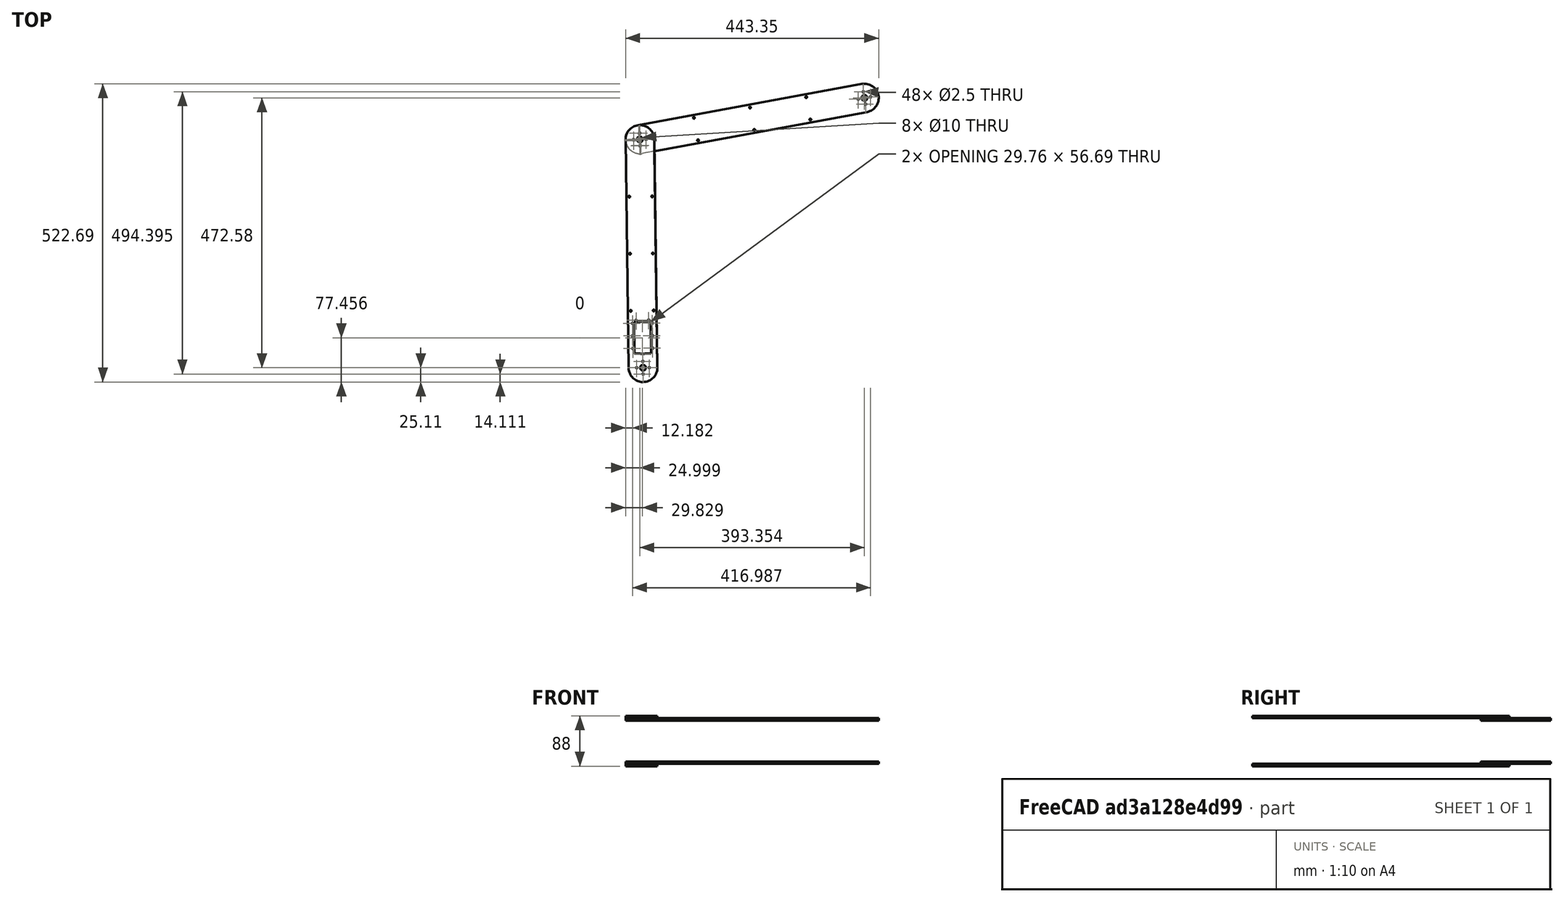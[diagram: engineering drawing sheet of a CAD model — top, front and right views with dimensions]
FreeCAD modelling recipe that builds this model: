
FCSTD DOCUMENT  (FreeCAD 1.0R39109 (Git))
Label: arm_assembly4
License: All rights reserved
LicenseURL: https://en.wikipedia.org/wiki/All_rights_reserved
objects: App::FeaturePython×14, App::Link×8, Sketcher::SketchObject×4, PartDesign::Pad×4, PartDesign::Body×4, Assembly::JointGroup×1, Assembly::AssemblyObject×1
note: 24 computed .brp shape members not serialized (recipe doc carries the construction recipe); baked Part::Feature solids carry a one-line shape summary decoded from their .brp
EXTERNAL_REF file=srv.FCStd obj=Part__Feature
EXTERNAL_REF file=pulleys/gt2_24T_pulley_open.FCStd obj=Body
EXTERNAL_REF file=pulleys/gt2_48T_pulley.FCStd obj=Body
EXTERNAL_REF file=pulleys/gt2_48T_pulley_double.FCStd obj=Body

FEATURE [Sketcher::SketchObject] Sketch
  ArcFitTolerance = 1e-06
  AttachmentSupport = -> [XY_Plane]
  FullyConstrained = false
  MakeInternals = false
  MapMode = 5
  sketch-geometry (67):
    g0: LineSegment [constr] StartX=1.5008e-12 StartY=20 StartZ=0 EndX=1.5008e-12 EndY=-20 EndZ=0
    g1: LineSegment [constr] StartX=-2.359e-12 StartY=0 StartZ=0 EndX=-2.359e-12 EndY=400 EndZ=0
    g2: LineSegment [constr] StartX=1.5008e-12 StartY=20 StartZ=0 EndX=1.5008e-12 EndY=25 EndZ=0
    g3: Circle CenterX=-2.359e-12 CenterY=400 CenterZ=0 NormalX=0 NormalY=0 NormalZ=1 AngleXU=0 Radius=5
    g4: Circle CenterX=-2.359e-12 CenterY=400 CenterZ=0 NormalX=0 NormalY=0 NormalZ=1 AngleXU=0 Radius=2
    g5: Circle CenterX=-10.9997 CenterY=400 CenterZ=0 NormalX=0 NormalY=0 NormalZ=1 AngleXU=0 Radius=1.25
    g6: Circle CenterX=0 CenterY=389 CenterZ=0 NormalX=0 NormalY=0 NormalZ=1 AngleXU=0 Radius=1.25
    g7: Circle CenterX=10.9997 CenterY=400 CenterZ=0 NormalX=0 NormalY=0 NormalZ=1 AngleXU=0 Radius=1.25
    g8: Circle CenterX=0 CenterY=411 CenterZ=0 NormalX=0 NormalY=0 NormalZ=1 AngleXU=0 Radius=1.25
    g9: LineSegment [constr] StartX=0 StartY=-5 StartZ=0 EndX=0 EndY=5.99996 EndZ=0
    g10: Circle [constr] CenterX=0 CenterY=0 CenterZ=0 NormalX=0 NormalY=0 NormalZ=1 AngleXU=0 Radius=14
    g11: LineSegment [constr] StartX=0 StartY=0 StartZ=0 EndX=25.23 EndY=0 EndZ=0
    g12: Circle [constr] CenterX=0 CenterY=-3.8e-05 CenterZ=0 NormalX=0 NormalY=0 NormalZ=1 AngleXU=0 Radius=11
    g13: Circle CenterX=0 CenterY=0 CenterZ=0 NormalX=0 NormalY=0 NormalZ=1 AngleXU=0 Radius=5
    g14: Circle CenterX=10.9997 CenterY=0 CenterZ=0 NormalX=0 NormalY=0 NormalZ=1 AngleXU=0 Radius=1.25
    g15: Circle CenterX=-10.9997 CenterY=0 CenterZ=0 NormalX=0 NormalY=0 NormalZ=1 AngleXU=0 Radius=1.25
    g16: Circle CenterX=0 CenterY=-10.9997 CenterZ=0 NormalX=0 NormalY=0 NormalZ=1 AngleXU=0 Radius=1.25
    g17: Circle CenterX=0 CenterY=11 CenterZ=0 NormalX=0 NormalY=0 NormalZ=1 AngleXU=0 Radius=1.25
    g18: LineSegment [constr] StartX=0 StartY=0 StartZ=0 EndX=-25 EndY=0 EndZ=0
    g19: LineSegment [constr] StartX=20.1368 StartY=86.0999 StartZ=0 EndX=20.1368 EndY=24.9999 EndZ=0
    g20: LineSegment [constr] StartX=0.036848 StartY=80.5 StartZ=0 EndX=14.5368 EndY=80.5 EndZ=0
    g21: LineSegment StartX=14.5368 StartY=80.5 StartZ=0 EndX=-14.4632 EndY=80.5 EndZ=0
    g22: LineSegment StartX=14.5368 StartY=80.5 StartZ=0 EndX=14.5368 EndY=24.9999 EndZ=0
    g23: Circle CenterX=11.0368 CenterY=83.3 CenterZ=0 NormalX=0 NormalY=0 NormalZ=1 AngleXU=0 Radius=1.25
    g24: Circle CenterX=17.3368 CenterY=78 CenterZ=0 NormalX=0 NormalY=0 NormalZ=1 AngleXU=0 Radius=1.25
    g25: LineSegment [constr] StartX=-20.0632 StartY=86.0999 StartZ=0 EndX=20.1368 EndY=86.0999 EndZ=0
    g26: Circle CenterX=17.3368 CenterY=56 CenterZ=0 NormalX=0 NormalY=0 NormalZ=1 AngleXU=0 Radius=1.25
    g27: Circle CenterX=17.3368 CenterY=34 CenterZ=0 NormalX=0 NormalY=0 NormalZ=1 AngleXU=0 Radius=1.25
    g28: Circle [constr] CenterX=0.036848 CenterY=37.9999 CenterZ=0 NormalX=0 NormalY=0 NormalZ=1 AngleXU=0 Radius=14
    g29: ArcOfCircle CenterX=0.036848 CenterY=37.9999 CenterZ=0 NormalX=0 NormalY=0 NormalZ=1 AngleXU=0 Radius=14 StartAngle=4.33214 EndAngle=5.09264
    g30: LineSegment StartX=5.233 StartY=24.9999 StartZ=0 EndX=14.5368 EndY=24.9999 EndZ=0
    g31: LineSegment [constr] StartX=14.5368 StartY=24.9999 StartZ=0 EndX=20.1368 EndY=24.9999 EndZ=0
    g32: LineSegment [constr] StartX=17.3368 StartY=56 StartZ=0 EndX=-17.2632 EndY=56 EndZ=0
    g33: LineSegment [constr] StartX=-20.0632 StartY=24.9999 StartZ=0 EndX=-20.0632 EndY=86.0999 EndZ=0
    g34: LineSegment StartX=-14.4632 StartY=80.5 StartZ=0 EndX=-14.4632 EndY=24.9999 EndZ=0
    g35: Circle CenterX=-17.2632 CenterY=78 CenterZ=0 NormalX=0 NormalY=0 NormalZ=1 AngleXU=0 Radius=1.25
    g36: Circle CenterX=-10.9632 CenterY=83.3 CenterZ=0 NormalX=0 NormalY=0 NormalZ=1 AngleXU=0 Radius=1.25
    g37: Circle CenterX=-17.2632 CenterY=56 CenterZ=0 NormalX=0 NormalY=0 NormalZ=1 AngleXU=0 Radius=1.25
    g38: Circle CenterX=-17.2632 CenterY=34 CenterZ=0 NormalX=0 NormalY=0 NormalZ=1 AngleXU=0 Radius=1.25
    g39: LineSegment StartX=-14.4632 StartY=24.9999 StartZ=0 EndX=-5.15931 EndY=24.9999 EndZ=0
    g40: LineSegment [constr] StartX=-20.0632 StartY=24.9999 StartZ=0 EndX=-14.4632 EndY=24.9999 EndZ=0
    g41: ArcOfCircle CenterX=0.115002 CenterY=3.75548e-06 CenterZ=0 NormalX=0 NormalY=0 NormalZ=1 AngleXU=0 Radius=25.115 StartAngle=3.14159 EndAngle=6.28319
    g42: ArcOfCircle CenterX=0.115002 CenterY=399.959 CenterZ=0 NormalX=0 NormalY=0 NormalZ=1 AngleXU=0 Radius=25.115 StartAngle=0 EndAngle=3.14159
    g43: LineSegment StartX=-25 StartY=3.75548e-06 StartZ=0 EndX=-25 EndY=399.959 EndZ=0
    g44: LineSegment StartX=25.23 StartY=3.75548e-06 StartZ=0 EndX=25.23 EndY=399.959 EndZ=0
    g45: LineSegment [constr] StartX=25.23 StartY=199.98 StartZ=0 EndX=-25 EndY=199.98 EndZ=0
    g46: LineSegment [constr] StartX=25.23 StartY=199.98 StartZ=0 EndX=55.23 EndY=199.98 EndZ=0
    g47: LineSegment [constr] StartX=25.23 StartY=0 StartZ=0 EndX=55.23 EndY=0 EndZ=0
    g48: LineSegment [constr] StartX=55.23 StartY=0 StartZ=0 EndX=55.23 EndY=199.98 EndZ=0
    g49: LineSegment [constr] StartX=55.23 StartY=99.9898 StartZ=0 EndX=25.23 EndY=99.9898 EndZ=0
    g50: LineSegment [constr] StartX=25.23 StartY=99.9898 StartZ=0 EndX=-25 EndY=99.9898 EndZ=0
    g51: LineSegment [constr] StartX=25.23 StartY=399.959 StartZ=0 EndX=55.23 EndY=399.959 EndZ=0
    g52: LineSegment [constr] StartX=55.23 StartY=399.959 StartZ=0 EndX=55.23 EndY=199.98 EndZ=0
    g53: LineSegment [constr] StartX=55.23 StartY=299.969 StartZ=0 EndX=25.23 EndY=299.969 EndZ=0
    g54: LineSegment [constr] StartX=25.23 StartY=299.969 StartZ=0 EndX=-25 EndY=299.969 EndZ=0
    g55: LineSegment [constr] StartX=-25 StartY=299.969 StartZ=0 EndX=-20 EndY=299.969 EndZ=0
    g56: LineSegment [constr] StartX=-20 StartY=299.969 StartZ=0 EndX=-20 EndY=199.98 EndZ=0
    g57: LineSegment [constr] StartX=-20 StartY=199.98 StartZ=0 EndX=-20 EndY=99.9898 EndZ=0
    g58: LineSegment [constr] StartX=25.23 StartY=299.969 StartZ=0 EndX=20.23 EndY=299.969 EndZ=0
    g59: LineSegment [constr] StartX=20.23 StartY=299.969 StartZ=0 EndX=20.23 EndY=199.98 EndZ=0
    g60: LineSegment [constr] StartX=20.23 StartY=199.98 StartZ=0 EndX=20.23 EndY=99.9898 EndZ=0
    g61: Circle CenterX=-20 CenterY=299.969 CenterZ=0 NormalX=0 NormalY=0 NormalZ=1 AngleXU=0 Radius=1.5
    g62: Circle CenterX=20.23 CenterY=299.969 CenterZ=0 NormalX=0 NormalY=0 NormalZ=1 AngleXU=0 Radius=1.5
    g63: Circle CenterX=-20 CenterY=199.98 CenterZ=0 NormalX=0 NormalY=0 NormalZ=1 AngleXU=0 Radius=1.5
    g64: Circle CenterX=20.23 CenterY=199.98 CenterZ=0 NormalX=0 NormalY=0 NormalZ=1 AngleXU=0 Radius=1.5
    g65: Circle CenterX=-20 CenterY=99.9898 CenterZ=0 NormalX=0 NormalY=0 NormalZ=1 AngleXU=0 Radius=1.5
    g66: Circle CenterX=20.23 CenterY=99.9898 CenterZ=0 NormalX=0 NormalY=0 NormalZ=1 AngleXU=0 Radius=1.5
  constraints (132):
    c: Vertical(g0)
    c: Vertical(g1)
    c: Coincident(g2,g0)
    c: Vertical(g2)
    c: Diameter(g3) = 10
    c: Coincident(g3,g1)
    c: Diameter(g4) = 4
    c: Coincident(g4,g1)
    c: Diameter(g8) = 2.5
    c: Diameter(g5) = 2.5
    c: Diameter(g6) = 2.5
    c: Diameter(g7) = 2.5
    c: Vertical(g9)
    c: Diameter(g10) = 28
    c: Coincident(g18,g10)
    c: Horizontal(g18)
    c: Coincident(g11,g10)
    c: Horizontal(g11)
    c: Diameter(g12) = 22
    c: Diameter(g13) = 10
    c: Coincident(g13,g10)
    c: Diameter(g17) = 2.5
    c: Diameter(g15) = 2.5
    c: Diameter(g16) = 2.5
    c: Diameter(g14) = 2.5
    c: Coincident(g25,g19)
    c: Coincident(g33,g25)
    c: Horizontal(g25)
    c: Vertical(g19)
    c: Vertical(g33)
    c: Distance(g19,g33) = 40.2
    c: Distance(g25,g33) = 61.1
    c: Diameter(g29) = 28
    c: Horizontal(g20)
    c: Coincident(g21,g20)
    c: Horizontal(g21)
    c: Coincident(g34,g21)
    c: Vertical(g34)
    c: Coincident(g22,g20)
    c: Vertical(g22)
    c: Diameter(g23) = 2.5
    c: Equal(g23,g36)
    c: Equal(g23,g27)
    c: Equal(g23,g38)
    c: Equal(g23,g37)
    c: Equal(g23,g35)
    c: Equal(g23,g24)
    c: Equal(g23,g26)
    c: Coincident(g28,g29)
    c: PointOnObject(g29,g28)
    c: Coincident(g30,g29)
    c: Coincident(g30,g22)
    c: Horizontal(g30)
    c: Coincident(g31,g22)
    c: Coincident(g31,g19)
    c: Horizontal(g31)
    c: Coincident(g39,g34)
    c: Coincident(g39,g29)
    c: Horizontal(g39)
    c: Coincident(g40,g33)
    c: Coincident(g40,g34)
    c: Horizontal(g40)
    c: Coincident(g32,g26)
    c: Coincident(g32,g37)
    c: Horizontal(g32)
    c: DistanceY(g28,g1) = 362
    c: Tangent(g41,g43) = 1.5708
    c: Tangent(g41,g44) = -1.5708
    c: Tangent(g42,g43) = 1.5708
    c: Tangent(g42,g44) = -1.5708
    c: Equal(g41,g42)
    c: Symmetric(g44,g44,g45)
    c: Symmetric(g43,g43,g45)
    c: Horizontal(g45)
    c: Distance(g46) = 30
    c: Horizontal(g46)
    c: Coincident(g46,g45)
    c: Distance(g47) = 30
    c: Horizontal(g47)
    c: Coincident(g47,g11)
    c: PointOnObject(g47,g-1)
    c: Coincident(g48,g47)
    c: Coincident(g48,g46)
    c: Vertical(g48)
    c: Symmetric(g48,g48,g49)
    c: PointOnObject(g49,g44)
    c: Horizontal(g49)
    c: Coincident(g50,g49)
    c: PointOnObject(g50,g43)
    c: Horizontal(g50)
    c: Distance(g51) = 30
    c: Horizontal(g51)
    c: Coincident(g51,g42)
    c: Coincident(g52,g51)
    c: Coincident(g52,g46)
    c: Symmetric(g52,g52,g53)
    c: PointOnObject(g53,g44)
    c: Horizontal(g53)
    c: Coincident(g54,g53)
    c: PointOnObject(g54,g43)
    c: Horizontal(g54)
    c: Distance(g55) = 5
    c: Coincident(g55,g54)
    c: PointOnObject(g55,g54)
    c: Coincident(g56,g55)
    c: PointOnObject(g56,g45)
    c: Vertical(g56)
    c: Coincident(g57,g56)
    c: PointOnObject(g57,g50)
    c: Vertical(g57)
    c: Distance(g58) = 5
    c: Coincident(g58,g53)
    c: PointOnObject(g58,g54)
    c: Coincident(g59,g58)
    c: PointOnObject(g59,g45)
    c: Vertical(g59)
    c: Coincident(g60,g59)
    c: PointOnObject(g60,g50)
    c: Vertical(g60)
    c: Coincident(g61,g55)
    c: Diameter(g61) = 3
    c: Coincident(g62,g58)
    c: Equal(g61,g62)
    c: Coincident(g63,g56)
    c: Equal(g61,g63)
    c: Coincident(g64,g59)
    c: Equal(g63,g64)
    c: Coincident(g65,g57)
    c: Equal(g63,g65)
    c: Coincident(g66,g60)
    c: Equal(g65,g66)
    c: DistanceY(g41,g28) = 37.9999
FEATURE [Sketcher::SketchObject] Sketch001
  ArcFitTolerance = 1e-06
  FullyConstrained = false
  MakeInternals = false
  MapMode = 5
  sketch-geometry (41):
    g0: Circle [constr] CenterX=7e-16 CenterY=0.000303 CenterZ=0 NormalX=0 NormalY=0 NormalZ=1 AngleXU=0 Radius=14
    g1: LineSegment [constr] StartX=7e-16 StartY=0.000303 StartZ=0 EndX=7e-16 EndY=400.001 EndZ=0
    g2: Circle CenterX=7e-16 CenterY=400.001 CenterZ=0 NormalX=0 NormalY=0 NormalZ=1 AngleXU=0 Radius=5
    g3: Circle CenterX=7e-16 CenterY=0 CenterZ=0 NormalX=0 NormalY=0 NormalZ=1 AngleXU=0 Radius=5
    g4: Circle CenterX=7e-16 CenterY=400.001 CenterZ=0 NormalX=0 NormalY=0 NormalZ=1 AngleXU=0 Radius=2
    g5: Circle CenterX=7e-16 CenterY=0.000303 CenterZ=0 NormalX=0 NormalY=0 NormalZ=1 AngleXU=0 Radius=2
    g6: Circle [constr] CenterX=0 CenterY=0 CenterZ=0 NormalX=0 NormalY=0 NormalZ=1 AngleXU=0 Radius=11
    g7: ArcOfCircle CenterX=7e-16 CenterY=0 CenterZ=0 NormalX=0 NormalY=0 NormalZ=1 AngleXU=0 Radius=25 StartAngle=3.14159 EndAngle=6.28319
    g8: ArcOfCircle CenterX=7e-16 CenterY=400.001 CenterZ=0 NormalX=0 NormalY=0 NormalZ=1 AngleXU=0 Radius=25 StartAngle=6e-16 EndAngle=3.14159
    g9: LineSegment StartX=-25 StartY=-8e-15 StartZ=0 EndX=-25 EndY=400.001 EndZ=0
    g10: LineSegment StartX=25 StartY=0 StartZ=0 EndX=25 EndY=400.001 EndZ=0
    g11: Circle CenterX=10.9997 CenterY=400.001 CenterZ=0 NormalX=0 NormalY=0 NormalZ=1 AngleXU=0 Radius=1.25
    g12: Circle CenterX=0 CenterY=411.001 CenterZ=0 NormalX=0 NormalY=0 NormalZ=1 AngleXU=0 Radius=1.25
    g13: Circle CenterX=-10.9997 CenterY=400.001 CenterZ=0 NormalX=0 NormalY=0 NormalZ=1 AngleXU=0 Radius=1.25
    g14: Circle CenterX=0 CenterY=389.001 CenterZ=0 NormalX=0 NormalY=0 NormalZ=1 AngleXU=0 Radius=1.25
    g15: Circle CenterX=10.9997 CenterY=0.000303 CenterZ=0 NormalX=0 NormalY=0 NormalZ=1 AngleXU=0 Radius=1.25
    g16: Circle CenterX=0 CenterY=11 CenterZ=0 NormalX=0 NormalY=0 NormalZ=1 AngleXU=0 Radius=1.25
    g17: Circle CenterX=-10.9997 CenterY=0.000303 CenterZ=0 NormalX=0 NormalY=0 NormalZ=1 AngleXU=0 Radius=1.25
    g18: Circle CenterX=0 CenterY=-10.9994 CenterZ=0 NormalX=0 NormalY=0 NormalZ=1 AngleXU=0 Radius=1.25
    g19: LineSegment [constr] StartX=25 StartY=200 StartZ=0 EndX=-25 EndY=200 EndZ=0
    g20: LineSegment [constr] StartX=25 StartY=200 StartZ=0 EndX=55 EndY=200 EndZ=0
    g21: LineSegment [constr] StartX=25 StartY=0 StartZ=0 EndX=55 EndY=0 EndZ=0
    g22: LineSegment [constr] StartX=25 StartY=400.001 StartZ=0 EndX=55 EndY=400.001 EndZ=0
    g23: LineSegment [constr] StartX=55 StartY=200 StartZ=0 EndX=55 EndY=400.001 EndZ=0
    g24: LineSegment [constr] StartX=55 StartY=200 StartZ=0 EndX=55 EndY=0 EndZ=0
    g25: LineSegment [constr] StartX=55 StartY=100 StartZ=0 EndX=25 EndY=100 EndZ=0
    g26: LineSegment [constr] StartX=25 StartY=100 StartZ=0 EndX=-25 EndY=100 EndZ=0
    g27: LineSegment [constr] StartX=55 StartY=300 StartZ=0 EndX=25 EndY=300 EndZ=0
    g28: LineSegment [constr] StartX=25 StartY=300 StartZ=0 EndX=-25 EndY=300 EndZ=0
    g29: LineSegment [constr] StartX=-25 StartY=300 StartZ=0 EndX=-20 EndY=300 EndZ=0
    g30: LineSegment [constr] StartX=-20 StartY=300 StartZ=0 EndX=-20 EndY=200 EndZ=0
    g31: LineSegment [constr] StartX=-20 StartY=200 StartZ=0 EndX=-20 EndY=100 EndZ=0
    g32: LineSegment [constr] StartX=25 StartY=100 StartZ=0 EndX=20 EndY=100 EndZ=0
    g33: LineSegment [constr] StartX=20 StartY=100 StartZ=0 EndX=20 EndY=200 EndZ=0
    g34: LineSegment [constr] StartX=20 StartY=200 StartZ=0 EndX=20 EndY=300 EndZ=0
    g35: Circle CenterX=-20 CenterY=300 CenterZ=0 NormalX=0 NormalY=0 NormalZ=1 AngleXU=0 Radius=1.5
    g36: Circle CenterX=20 CenterY=300 CenterZ=0 NormalX=0 NormalY=0 NormalZ=1 AngleXU=0 Radius=1.5
    g37: Circle CenterX=-20 CenterY=200 CenterZ=0 NormalX=0 NormalY=0 NormalZ=1 AngleXU=0 Radius=1.5
    g38: Circle CenterX=20 CenterY=200 CenterZ=0 NormalX=0 NormalY=0 NormalZ=1 AngleXU=0 Radius=1.5
    g39: Circle CenterX=-20 CenterY=100 CenterZ=0 NormalX=0 NormalY=0 NormalZ=1 AngleXU=0 Radius=1.5
    g40: Circle CenterX=20 CenterY=100 CenterZ=0 NormalX=0 NormalY=0 NormalZ=1 AngleXU=0 Radius=1.5
  constraints (85):
    c: Diameter(g0) = 28
    c: Coincident(g1,g0)
    c: Vertical(g1)
    c: Coincident(g2,g1)
    c: Diameter(g3) = 10
    c: Diameter(g4) = 4
    c: Coincident(g4,g1)
    c: Diameter(g5) = 4
    c: Coincident(g5,g0)
    c: Diameter(g6) = 22
    c: Tangent(g7,g9) = 1.5708
    c: Tangent(g7,g10) = -1.5708
    c: Tangent(g8,g9) = 1.5708
    c: Tangent(g8,g10) = -1.5708
    c: Equal(g7,g8)
    c: Radius(g7) = 25
    c: Coincident(g7,g3)
    c: Coincident(g8,g1)
    c: Vertical(g9)
    c: Diameter(g12) = 2.5
    c: Diameter(g13) = 2.5
    c: Diameter(g14) = 2.5
    c: Diameter(g11) = 2.5
    c: Diameter(g16) = 2.5
    c: Diameter(g17) = 2.5
    c: Diameter(g18) = 2.5
    c: Diameter(g15) = 2.5
    c: Symmetric(g10,g10,g19)
    c: Symmetric(g9,g9,g19)
    c: Distance(g20) = 30
    c: Horizontal(g20)
    c: Coincident(g20,g19)
    c: Distance(g21) = 30
    c: Horizontal(g21)
    c: Coincident(g21,g7)
    c: PointOnObject(g21,g-1)
    c: Distance(g22) = 30
    c: Horizontal(g22)
    c: Coincident(g22,g8)
    c: Coincident(g23,g20)
    c: Coincident(g23,g22)
    c: Coincident(g24,g20)
    c: Coincident(g24,g21)
    c: Symmetric(g24,g24,g25)
    c: PointOnObject(g25,g10)
    c: Horizontal(g25)
    c: Coincident(g26,g25)
    c: PointOnObject(g26,g9)
    c: Horizontal(g26)
    c: Symmetric(g23,g23,g27)
    c: PointOnObject(g27,g10)
    c: Horizontal(g27)
    c: Coincident(g28,g27)
    c: PointOnObject(g28,g9)
    c: Horizontal(g28)
    c: Distance(g29) = 5
    c: Horizontal(g29)
    c: Coincident(g29,g28)
    c: Coincident(g30,g29)
    c: PointOnObject(g30,g19)
    c: Vertical(g30)
    c: Coincident(g31,g30)
    c: PointOnObject(g31,g26)
    c: Vertical(g31)
    c: Distance(g32) = 5
    c: Horizontal(g32)
    c: Coincident(g32,g25)
    c: Coincident(g33,g32)
    c: PointOnObject(g33,g19)
    c: Vertical(g33)
    c: Coincident(g34,g33)
    c: PointOnObject(g34,g28)
    c: Vertical(g34)
    c: Diameter(g35) = 3
    c: Coincident(g35,g29)
    c: Coincident(g36,g34)
    c: Equal(g35,g36)
    c: Coincident(g37,g30)
    c: Equal(g35,g37)
    c: Coincident(g38,g33)
    c: Equal(g37,g38)
    c: Coincident(g39,g31)
    c: Equal(g37,g39)
    c: Coincident(g40,g32)
    c: Equal(g39,g40)
FEATURE [PartDesign::Pad] Pad
  Direction = (0,0,1)
  Length = 4
  Length2 = 10
  Profile = -> Sketch
  ReferenceAxis = -> Sketch [N_Axis]
  Refine = true
  Suppressed = false
  Type = 0
FEATURE [PartDesign::Body] Body  label="arm_low_1"
  AllowCompound = false
  Group = -> [Sketch,Pad]
  Origin = -> Origin
  Placement = pos=(0,0,25.3) rot=(0,0,1;0.013804rad)
  Tip = -> Pad
FEATURE [PartDesign::Pad] Pad001
  Direction = (0,0,1)
  Length = 4
  Length2 = 10
  Profile = -> Sketch001
  ReferenceAxis = -> Sketch001 [N_Axis]
  Refine = true
  Suppressed = false
  Type = 0
FEATURE [PartDesign::Body] Body001  label="arm_high_1"
  AllowCompound = false
  Group = -> [Sketch001,Pad001]
  Origin = -> Origin001
  Placement = pos=(387.832,472.58,29.3) rot=(0,0,1;1.75335rad)
  Tip = -> Pad001
FEATURE [App::Link] DC05_M01_DUMMY
  LinkedObject = -> <external srv.FCStd>#Part__Feature
FEATURE [App::FeaturePython] GroundedJoint  # Assembly grounded joint (typed FeaturePython)
  ObjectToGround = -> DC05_M01_DUMMY
FEATURE [App::FeaturePython] Joint  label="Revolute"  # Assembly joint (typed FeaturePython)
  Activated = true
  AngleMax = 0
  AngleMin = 0
  Detach1 = false
  Detach2 = false
  Distance = 0
  Distance2 = 0
  EnableAngleMax = false
  EnableAngleMin = false
  EnableLengthMax = false
  EnableLengthMin = false
  JointType = 1 (Revolute)
  LengthMax = 0
  LengthMin = 0
  Placement2 = pos=(0,0,25.3) rot=(-0.707107,0.707107,0;3.14159rad)
  Reference1 = -> Assembly [Body.Face11,Body.Edge2]
  Reference2 = -> Assembly [DC05_M01_DUMMY.Face269,DC05_M01_DUMMY.Edge1]
FEATURE [App::FeaturePython] Joint001  label="Revolute001"  # Assembly joint (typed FeaturePython)
  Activated = true
  AngleMax = 0
  AngleMin = 0
  Detach1 = false
  Detach2 = false
  Distance = 0
  Distance2 = 0
  EnableAngleMax = false
  EnableAngleMin = false
  EnableLengthMax = false
  EnableLengthMin = false
  JointType = 1 (Revolute)
  LengthMax = 0
  LengthMin = 0
  Placement1 = pos=(5.68e-14,400.001,0) rot=(0,0,1;0rad)
  Placement2 = pos=(-2.3554e-12,400,4) rot=(0,0,1;0rad)
  Reference1 = -> Assembly [Body001.Edge17,Body001.Edge17]
  Reference2 = -> Assembly [Body.Edge36,Body.Edge36]
FEATURE [App::Link] DC05_M01_DUMMY001
  LinkPlacement = pos=(-0.487674,37.9968,9.05) rot=(0,0,1;3.1554rad)
  LinkedObject = -> <external srv.FCStd>#Part__Feature
  Placement = pos=(-0.487674,37.9968,9.05) rot=(0,0,1;3.1554rad)
FEATURE [App::FeaturePython] Joint002  label="Distance"  # Assembly joint (typed FeaturePython)
  Activated = true
  AngleMax = 0
  AngleMin = 0
  Detach1 = false
  Detach2 = false
  Distance = 0
  Distance2 = 0
  EnableAngleMax = false
  EnableAngleMin = false
  EnableLengthMax = false
  EnableLengthMin = false
  JointType = 5 (Distance)
  LengthMax = 0
  LengthMin = 0
  Placement1 = pos=(0.00149626,-23.2403,17) rot=(0,0,1;0rad)
  Placement2 = pos=(-10.9997,1e-16,2) rot=(0,0,1;0rad)
  Reference1 = -> Assembly [DC05_M01_DUMMY001.Face128,DC05_M01_DUMMY001.Vertex405]
  Reference2 = -> Assembly [Body.Face29,Body.Edge23]
FEATURE [App::FeaturePython] Joint003  label="Distance001"  # Assembly joint (typed FeaturePython)
  Activated = true
  AngleMax = 0
  AngleMin = 0
  Detach1 = false
  Detach2 = false
  Distance = -55.5
  Distance2 = 0
  EnableAngleMax = false
  EnableAngleMin = false
  EnableLengthMax = false
  EnableLengthMin = false
  JointType = 5 (Distance)
  LengthMax = 0
  LengthMin = 0
  Placement1 = pos=(3.76754e-09,-42.5,18.25) rot=(1,0,0;1.5708rad)
  Placement2 = pos=(-9.81123,24.9999,2) rot=(-1,0,0;1.5708rad)
  Reference1 = -> Assembly [DC05_M01_DUMMY001.Face34,DC05_M01_DUMMY001.Face34]
  Reference2 = -> Assembly [Body.Face7,Body.Face7]
FEATURE [App::FeaturePython] Joint004  label="Distance002"  # Assembly joint (typed FeaturePython)
  Activated = true
  AngleMax = 0
  AngleMin = 0
  Detach1 = false
  Detach2 = false
  Distance = -28.5
  Distance2 = 0
  EnableAngleMax = false
  EnableAngleMin = false
  EnableLengthMax = false
  EnableLengthMin = false
  JointType = 5 (Distance)
  LengthMax = 0
  LengthMin = 0
  Placement1 = pos=(-14.5,-15.25,18.25) rot=(0.57735,-0.57735,-0.57735;2.0944rad)
  Placement2 = pos=(0.036848,37.9999,2) rot=(0,0,1;0rad)
  Reference1 = -> Assembly [DC05_M01_DUMMY001.Face46,DC05_M01_DUMMY001.Face46]
  Reference2 = -> Assembly [Body.Face8,Body.Face8]
FEATURE [App::Link] Body002  label="Body"
  LinkPlacement = pos=(-0.487674,37.9968,38.55) rot=(0,0,1;4.72619rad)
  LinkedObject = -> <external pulleys/gt2_24T_pulley_open.FCStd>#Body
  Placement = pos=(-0.487674,37.9968,38.55) rot=(0,0,1;4.72619rad)
FEATURE [App::FeaturePython] Joint005  label="Fixed"  # Assembly joint (typed FeaturePython)
  Activated = true
  AngleMax = 0
  AngleMin = 0
  Detach1 = false
  Detach2 = false
  Distance = 0
  Distance2 = 0
  EnableAngleMax = false
  EnableAngleMin = false
  EnableLengthMax = false
  EnableLengthMin = false
  JointType = 0 (Fixed)
  LengthMax = 0
  LengthMin = 0
  Placement1 = pos=(0,0,-6) rot=(-1,0,0;3.14159rad)
  Placement2 = pos=(0,0,23.5) rot=(-0.707107,-0.707107,0;3.14159rad)
  Reference1 = -> Assembly [Body002.Edge529,Body002.Edge529]
  Reference2 = -> Assembly [DC05_M01_DUMMY001.Edge888,DC05_M01_DUMMY001.Edge888]
FEATURE [App::Link] Body003
  LinkPlacement = pos=(-5.52126,399.962,35.3) rot=(0,0,1;1.75335rad)
  LinkedObject = -> <external pulleys/gt2_48T_pulley.FCStd>#Body
  Placement = pos=(-5.52126,399.962,35.3) rot=(0,0,1;1.75335rad)
FEATURE [App::FeaturePython] Joint006  label="Fixed001"  # Assembly joint (typed FeaturePython)
  Activated = true
  AngleMax = 0
  AngleMin = 0
  Detach1 = false
  Detach2 = false
  Distance = 0
  Distance2 = 0
  EnableAngleMax = false
  EnableAngleMin = false
  EnableLengthMax = false
  EnableLengthMin = false
  JointType = 0 (Fixed)
  LengthMax = 0
  LengthMin = 0
  Placement1 = pos=(0,0,-2) rot=(1,0,0;3.14159rad)
  Placement2 = pos=(5.68e-14,400.001,4) rot=(0,0,1;0rad)
  Reference1 = -> Assembly [Body003.Edge875,Body003.Edge875]
  Reference2 = -> Assembly [Body001.Edge18,Body001.Edge18]
FEATURE [Sketcher::SketchObject] Sketch002
  ArcFitTolerance = 1e-06
  AttachmentSupport = -> [XY_Plane004]
  FullyConstrained = false
  MakeInternals = false
  MapMode = 5
  sketch-geometry (67):
    g0: LineSegment [constr] StartX=1.5008e-12 StartY=20 StartZ=0 EndX=1.5008e-12 EndY=-20 EndZ=0
    g1: LineSegment [constr] StartX=-2.359e-12 StartY=0 StartZ=0 EndX=-2.359e-12 EndY=400 EndZ=0
    g2: LineSegment [constr] StartX=1.5008e-12 StartY=20 StartZ=0 EndX=1.5008e-12 EndY=25 EndZ=0
    g3: Circle CenterX=-2.359e-12 CenterY=400 CenterZ=0 NormalX=0 NormalY=0 NormalZ=1 AngleXU=0 Radius=5
    g4: Circle CenterX=-2.359e-12 CenterY=400 CenterZ=0 NormalX=0 NormalY=0 NormalZ=1 AngleXU=0 Radius=2
    g5: Circle CenterX=-10.9997 CenterY=400 CenterZ=0 NormalX=0 NormalY=0 NormalZ=1 AngleXU=0 Radius=1.25
    g6: Circle CenterX=0 CenterY=389 CenterZ=0 NormalX=0 NormalY=0 NormalZ=1 AngleXU=0 Radius=1.25
    g7: Circle CenterX=10.9997 CenterY=400 CenterZ=0 NormalX=0 NormalY=0 NormalZ=1 AngleXU=0 Radius=1.25
    g8: Circle CenterX=0 CenterY=411 CenterZ=0 NormalX=0 NormalY=0 NormalZ=1 AngleXU=0 Radius=1.25
    g9: LineSegment [constr] StartX=0 StartY=-5 StartZ=0 EndX=0 EndY=5.99996 EndZ=0
    g10: Circle [constr] CenterX=0 CenterY=0 CenterZ=0 NormalX=0 NormalY=0 NormalZ=1 AngleXU=0 Radius=14
    g11: LineSegment [constr] StartX=0 StartY=0 StartZ=0 EndX=25.23 EndY=0 EndZ=0
    g12: Circle [constr] CenterX=0 CenterY=-3.8e-05 CenterZ=0 NormalX=0 NormalY=0 NormalZ=1 AngleXU=0 Radius=11
    g13: Circle CenterX=0 CenterY=0 CenterZ=0 NormalX=0 NormalY=0 NormalZ=1 AngleXU=0 Radius=5
    g14: Circle CenterX=10.9997 CenterY=0 CenterZ=0 NormalX=0 NormalY=0 NormalZ=1 AngleXU=0 Radius=1.25
    g15: Circle CenterX=-10.9997 CenterY=0 CenterZ=0 NormalX=0 NormalY=0 NormalZ=1 AngleXU=0 Radius=1.25
    g16: Circle CenterX=0 CenterY=-10.9997 CenterZ=0 NormalX=0 NormalY=0 NormalZ=1 AngleXU=0 Radius=1.25
    g17: Circle CenterX=0 CenterY=11 CenterZ=0 NormalX=0 NormalY=0 NormalZ=1 AngleXU=0 Radius=1.25
    g18: LineSegment [constr] StartX=0 StartY=0 StartZ=0 EndX=-25 EndY=0 EndZ=0
    g19: LineSegment [constr] StartX=20.1368 StartY=86.0999 StartZ=0 EndX=20.1368 EndY=24.9999 EndZ=0
    g20: LineSegment [constr] StartX=0.036848 StartY=80.5 StartZ=0 EndX=14.5368 EndY=80.5 EndZ=0
    g21: LineSegment StartX=14.5368 StartY=80.5 StartZ=0 EndX=-14.4632 EndY=80.5 EndZ=0
    g22: LineSegment StartX=14.5368 StartY=80.5 StartZ=0 EndX=14.5368 EndY=24.9999 EndZ=0
    g23: Circle CenterX=11.0368 CenterY=83.3 CenterZ=0 NormalX=0 NormalY=0 NormalZ=1 AngleXU=0 Radius=1.25
    g24: Circle CenterX=17.3368 CenterY=78 CenterZ=0 NormalX=0 NormalY=0 NormalZ=1 AngleXU=0 Radius=1.25
    g25: LineSegment [constr] StartX=-20.0632 StartY=86.0999 StartZ=0 EndX=20.1368 EndY=86.0999 EndZ=0
    g26: Circle CenterX=17.3368 CenterY=56 CenterZ=0 NormalX=0 NormalY=0 NormalZ=1 AngleXU=0 Radius=1.25
    g27: Circle CenterX=17.3368 CenterY=34 CenterZ=0 NormalX=0 NormalY=0 NormalZ=1 AngleXU=0 Radius=1.25
    g28: Circle [constr] CenterX=0.036848 CenterY=37.9999 CenterZ=0 NormalX=0 NormalY=0 NormalZ=1 AngleXU=0 Radius=14
    g29: ArcOfCircle CenterX=0.036848 CenterY=37.9999 CenterZ=0 NormalX=0 NormalY=0 NormalZ=1 AngleXU=0 Radius=14 StartAngle=4.33214 EndAngle=5.09264
    g30: LineSegment StartX=5.233 StartY=24.9999 StartZ=0 EndX=14.5368 EndY=24.9999 EndZ=0
    g31: LineSegment [constr] StartX=14.5368 StartY=24.9999 StartZ=0 EndX=20.1368 EndY=24.9999 EndZ=0
    g32: LineSegment [constr] StartX=17.3368 StartY=56 StartZ=0 EndX=-17.2632 EndY=56 EndZ=0
    g33: LineSegment [constr] StartX=-20.0632 StartY=24.9999 StartZ=0 EndX=-20.0632 EndY=86.0999 EndZ=0
    g34: LineSegment StartX=-14.4632 StartY=80.5 StartZ=0 EndX=-14.4632 EndY=24.9999 EndZ=0
    g35: Circle CenterX=-17.2632 CenterY=78 CenterZ=0 NormalX=0 NormalY=0 NormalZ=1 AngleXU=0 Radius=1.25
    g36: Circle CenterX=-10.9632 CenterY=83.3 CenterZ=0 NormalX=0 NormalY=0 NormalZ=1 AngleXU=0 Radius=1.25
    g37: Circle CenterX=-17.2632 CenterY=56 CenterZ=0 NormalX=0 NormalY=0 NormalZ=1 AngleXU=0 Radius=1.25
    g38: Circle CenterX=-17.2632 CenterY=34 CenterZ=0 NormalX=0 NormalY=0 NormalZ=1 AngleXU=0 Radius=1.25
    g39: LineSegment StartX=-14.4632 StartY=24.9999 StartZ=0 EndX=-5.15931 EndY=24.9999 EndZ=0
    g40: LineSegment [constr] StartX=-20.0632 StartY=24.9999 StartZ=0 EndX=-14.4632 EndY=24.9999 EndZ=0
    g41: ArcOfCircle CenterX=0.115002 CenterY=3.75548e-06 CenterZ=0 NormalX=0 NormalY=0 NormalZ=1 AngleXU=0 Radius=25.115 StartAngle=3.14159 EndAngle=6.28319
    g42: ArcOfCircle CenterX=0.115002 CenterY=399.959 CenterZ=0 NormalX=0 NormalY=0 NormalZ=1 AngleXU=0 Radius=25.115 StartAngle=0 EndAngle=3.14159
    g43: LineSegment StartX=-25 StartY=3.75548e-06 StartZ=0 EndX=-25 EndY=399.959 EndZ=0
    g44: LineSegment StartX=25.23 StartY=3.75548e-06 StartZ=0 EndX=25.23 EndY=399.959 EndZ=0
    g45: LineSegment [constr] StartX=25.23 StartY=199.98 StartZ=0 EndX=-25 EndY=199.98 EndZ=0
    g46: LineSegment [constr] StartX=25.23 StartY=199.98 StartZ=0 EndX=55.23 EndY=199.98 EndZ=0
    g47: LineSegment [constr] StartX=25.23 StartY=0 StartZ=0 EndX=55.23 EndY=0 EndZ=0
    g48: LineSegment [constr] StartX=55.23 StartY=0 StartZ=0 EndX=55.23 EndY=199.98 EndZ=0
    g49: LineSegment [constr] StartX=55.23 StartY=99.9898 StartZ=0 EndX=25.23 EndY=99.9898 EndZ=0
    g50: LineSegment [constr] StartX=25.23 StartY=99.9898 StartZ=0 EndX=-25 EndY=99.9898 EndZ=0
    g51: LineSegment [constr] StartX=25.23 StartY=399.959 StartZ=0 EndX=55.23 EndY=399.959 EndZ=0
    g52: LineSegment [constr] StartX=55.23 StartY=399.959 StartZ=0 EndX=55.23 EndY=199.98 EndZ=0
    g53: LineSegment [constr] StartX=55.23 StartY=299.969 StartZ=0 EndX=25.23 EndY=299.969 EndZ=0
    g54: LineSegment [constr] StartX=25.23 StartY=299.969 StartZ=0 EndX=-25 EndY=299.969 EndZ=0
    g55: LineSegment [constr] StartX=-25 StartY=299.969 StartZ=0 EndX=-20 EndY=299.969 EndZ=0
    g56: LineSegment [constr] StartX=-20 StartY=299.969 StartZ=0 EndX=-20 EndY=199.98 EndZ=0
    g57: LineSegment [constr] StartX=-20 StartY=199.98 StartZ=0 EndX=-20 EndY=99.9898 EndZ=0
    g58: LineSegment [constr] StartX=25.23 StartY=299.969 StartZ=0 EndX=20.23 EndY=299.969 EndZ=0
    g59: LineSegment [constr] StartX=20.23 StartY=299.969 StartZ=0 EndX=20.23 EndY=199.98 EndZ=0
    g60: LineSegment [constr] StartX=20.23 StartY=199.98 StartZ=0 EndX=20.23 EndY=99.9898 EndZ=0
    g61: Circle CenterX=-20 CenterY=299.969 CenterZ=0 NormalX=0 NormalY=0 NormalZ=1 AngleXU=0 Radius=1.5
    g62: Circle CenterX=20.23 CenterY=299.969 CenterZ=0 NormalX=0 NormalY=0 NormalZ=1 AngleXU=0 Radius=1.5
    g63: Circle CenterX=-20 CenterY=199.98 CenterZ=0 NormalX=0 NormalY=0 NormalZ=1 AngleXU=0 Radius=1.5
    g64: Circle CenterX=20.23 CenterY=199.98 CenterZ=0 NormalX=0 NormalY=0 NormalZ=1 AngleXU=0 Radius=1.5
    g65: Circle CenterX=-20 CenterY=99.9898 CenterZ=0 NormalX=0 NormalY=0 NormalZ=1 AngleXU=0 Radius=1.5
    g66: Circle CenterX=20.23 CenterY=99.9898 CenterZ=0 NormalX=0 NormalY=0 NormalZ=1 AngleXU=0 Radius=1.5
  constraints (132):
    c: Vertical(g0)
    c: Vertical(g1)
    c: Coincident(g2,g0)
    c: Vertical(g2)
    c: Diameter(g3) = 10
    c: Coincident(g3,g1)
    c: Diameter(g4) = 4
    c: Coincident(g4,g1)
    c: Diameter(g8) = 2.5
    c: Diameter(g5) = 2.5
    c: Diameter(g6) = 2.5
    c: Diameter(g7) = 2.5
    c: Vertical(g9)
    c: Diameter(g10) = 28
    c: Coincident(g18,g10)
    c: Horizontal(g18)
    c: Coincident(g11,g10)
    c: Horizontal(g11)
    c: Diameter(g12) = 22
    c: Diameter(g13) = 10
    c: Coincident(g13,g10)
    c: Diameter(g17) = 2.5
    c: Diameter(g15) = 2.5
    c: Diameter(g16) = 2.5
    c: Diameter(g14) = 2.5
    c: Coincident(g25,g19)
    c: Coincident(g33,g25)
    c: Horizontal(g25)
    c: Vertical(g19)
    c: Vertical(g33)
    c: Distance(g19,g33) = 40.2
    c: Distance(g25,g33) = 61.1
    c: Diameter(g29) = 28
    c: Horizontal(g20)
    c: Coincident(g21,g20)
    c: Horizontal(g21)
    c: Coincident(g34,g21)
    c: Vertical(g34)
    c: Coincident(g22,g20)
    c: Vertical(g22)
    c: Diameter(g23) = 2.5
    c: Equal(g23,g36)
    c: Equal(g23,g27)
    c: Equal(g23,g38)
    c: Equal(g23,g37)
    c: Equal(g23,g35)
    c: Equal(g23,g24)
    c: Equal(g23,g26)
    c: Coincident(g28,g29)
    c: PointOnObject(g29,g28)
    c: Coincident(g30,g29)
    c: Coincident(g30,g22)
    c: Horizontal(g30)
    c: Coincident(g31,g22)
    c: Coincident(g31,g19)
    c: Horizontal(g31)
    c: Coincident(g39,g34)
    c: Coincident(g39,g29)
    c: Horizontal(g39)
    c: Coincident(g40,g33)
    c: Coincident(g40,g34)
    c: Horizontal(g40)
    c: Coincident(g32,g26)
    c: Coincident(g32,g37)
    c: Horizontal(g32)
    c: DistanceY(g28,g1) = 362
    c: Tangent(g41,g43) = 1.5708
    c: Tangent(g41,g44) = -1.5708
    c: Tangent(g42,g43) = 1.5708
    c: Tangent(g42,g44) = -1.5708
    c: Equal(g41,g42)
    c: Symmetric(g44,g44,g45)
    c: Symmetric(g43,g43,g45)
    c: Horizontal(g45)
    c: Distance(g46) = 30
    c: Horizontal(g46)
    c: Coincident(g46,g45)
    c: Distance(g47) = 30
    c: Horizontal(g47)
    c: Coincident(g47,g11)
    c: PointOnObject(g47,g-1)
    c: Coincident(g48,g47)
    c: Coincident(g48,g46)
    c: Vertical(g48)
    c: Symmetric(g48,g48,g49)
    c: PointOnObject(g49,g44)
    c: Horizontal(g49)
    c: Coincident(g50,g49)
    c: PointOnObject(g50,g43)
    c: Horizontal(g50)
    c: Distance(g51) = 30
    c: Horizontal(g51)
    c: Coincident(g51,g42)
    c: Coincident(g52,g51)
    c: Coincident(g52,g46)
    c: Symmetric(g52,g52,g53)
    c: PointOnObject(g53,g44)
    c: Horizontal(g53)
    c: Coincident(g54,g53)
    c: PointOnObject(g54,g43)
    c: Horizontal(g54)
    c: Distance(g55) = 5
    c: Coincident(g55,g54)
    c: PointOnObject(g55,g54)
    c: Coincident(g56,g55)
    c: PointOnObject(g56,g45)
    c: Vertical(g56)
    c: Coincident(g57,g56)
    c: PointOnObject(g57,g50)
    c: Vertical(g57)
    c: Distance(g58) = 5
    c: Coincident(g58,g53)
    c: PointOnObject(g58,g54)
    c: Coincident(g59,g58)
    c: PointOnObject(g59,g45)
    c: Vertical(g59)
    c: Coincident(g60,g59)
    c: PointOnObject(g60,g50)
    c: Vertical(g60)
    c: Coincident(g61,g55)
    c: Diameter(g61) = 3
    c: Coincident(g62,g58)
    c: Equal(g61,g62)
    c: Coincident(g63,g56)
    c: Equal(g61,g63)
    c: Coincident(g64,g59)
    c: Equal(g63,g64)
    c: Coincident(g65,g57)
    c: Equal(g63,g65)
    c: Coincident(g66,g60)
    c: Equal(g65,g66)
    c: DistanceY(g41,g28) = 37.9999
FEATURE [PartDesign::Pad] Pad002
  Direction = (0,0,1)
  Length = 4
  Length2 = 10
  Profile = -> Sketch002
  ReferenceAxis = -> Sketch002 [N_Axis]
  Refine = true
  Suppressed = false
  Type = 0
FEATURE [PartDesign::Body] Body004  label="arm_low_002"
  AllowCompound = false
  Group = -> [Sketch002,Pad002]
  Origin = -> Origin004
  Placement = pos=(0,0,109.3) rot=(0,0,1;0.013804rad)
  Tip = -> Pad002
FEATURE [Sketcher::SketchObject] Sketch003
  ArcFitTolerance = 1e-06
  FullyConstrained = false
  MakeInternals = false
  MapMode = 5
  sketch-geometry (41):
    g0: Circle [constr] CenterX=7e-16 CenterY=0.000303 CenterZ=0 NormalX=0 NormalY=0 NormalZ=1 AngleXU=0 Radius=14
    g1: LineSegment [constr] StartX=7e-16 StartY=0.000303 StartZ=0 EndX=7e-16 EndY=400.001 EndZ=0
    g2: Circle CenterX=7e-16 CenterY=400.001 CenterZ=0 NormalX=0 NormalY=0 NormalZ=1 AngleXU=0 Radius=5
    g3: Circle CenterX=7e-16 CenterY=0 CenterZ=0 NormalX=0 NormalY=0 NormalZ=1 AngleXU=0 Radius=5
    g4: Circle CenterX=7e-16 CenterY=400.001 CenterZ=0 NormalX=0 NormalY=0 NormalZ=1 AngleXU=0 Radius=2
    g5: Circle CenterX=7e-16 CenterY=0.000303 CenterZ=0 NormalX=0 NormalY=0 NormalZ=1 AngleXU=0 Radius=2
    g6: Circle [constr] CenterX=0 CenterY=0 CenterZ=0 NormalX=0 NormalY=0 NormalZ=1 AngleXU=0 Radius=11
    g7: ArcOfCircle CenterX=7e-16 CenterY=0 CenterZ=0 NormalX=0 NormalY=0 NormalZ=1 AngleXU=0 Radius=25 StartAngle=3.14159 EndAngle=6.28319
    g8: ArcOfCircle CenterX=7e-16 CenterY=400.001 CenterZ=0 NormalX=0 NormalY=0 NormalZ=1 AngleXU=0 Radius=25 StartAngle=6e-16 EndAngle=3.14159
    g9: LineSegment StartX=-25 StartY=-8e-15 StartZ=0 EndX=-25 EndY=400.001 EndZ=0
    g10: LineSegment StartX=25 StartY=0 StartZ=0 EndX=25 EndY=400.001 EndZ=0
    g11: Circle CenterX=10.9997 CenterY=400.001 CenterZ=0 NormalX=0 NormalY=0 NormalZ=1 AngleXU=0 Radius=1.25
    g12: Circle CenterX=0 CenterY=411.001 CenterZ=0 NormalX=0 NormalY=0 NormalZ=1 AngleXU=0 Radius=1.25
    g13: Circle CenterX=-10.9997 CenterY=400.001 CenterZ=0 NormalX=0 NormalY=0 NormalZ=1 AngleXU=0 Radius=1.25
    g14: Circle CenterX=0 CenterY=389.001 CenterZ=0 NormalX=0 NormalY=0 NormalZ=1 AngleXU=0 Radius=1.25
    g15: Circle CenterX=10.9997 CenterY=0.000303 CenterZ=0 NormalX=0 NormalY=0 NormalZ=1 AngleXU=0 Radius=1.25
    g16: Circle CenterX=0 CenterY=11 CenterZ=0 NormalX=0 NormalY=0 NormalZ=1 AngleXU=0 Radius=1.25
    g17: Circle CenterX=-10.9997 CenterY=0.000303 CenterZ=0 NormalX=0 NormalY=0 NormalZ=1 AngleXU=0 Radius=1.25
    g18: Circle CenterX=0 CenterY=-10.9994 CenterZ=0 NormalX=0 NormalY=0 NormalZ=1 AngleXU=0 Radius=1.25
    g19: LineSegment [constr] StartX=25 StartY=200 StartZ=0 EndX=-25 EndY=200 EndZ=0
    g20: LineSegment [constr] StartX=25 StartY=200 StartZ=0 EndX=55 EndY=200 EndZ=0
    g21: LineSegment [constr] StartX=25 StartY=0 StartZ=0 EndX=55 EndY=0 EndZ=0
    g22: LineSegment [constr] StartX=25 StartY=400.001 StartZ=0 EndX=55 EndY=400.001 EndZ=0
    g23: LineSegment [constr] StartX=55 StartY=200 StartZ=0 EndX=55 EndY=400.001 EndZ=0
    g24: LineSegment [constr] StartX=55 StartY=200 StartZ=0 EndX=55 EndY=0 EndZ=0
    g25: LineSegment [constr] StartX=55 StartY=100 StartZ=0 EndX=25 EndY=100 EndZ=0
    g26: LineSegment [constr] StartX=25 StartY=100 StartZ=0 EndX=-25 EndY=100 EndZ=0
    g27: LineSegment [constr] StartX=55 StartY=300 StartZ=0 EndX=25 EndY=300 EndZ=0
    g28: LineSegment [constr] StartX=25 StartY=300 StartZ=0 EndX=-25 EndY=300 EndZ=0
    g29: LineSegment [constr] StartX=-25 StartY=300 StartZ=0 EndX=-20 EndY=300 EndZ=0
    g30: LineSegment [constr] StartX=-20 StartY=300 StartZ=0 EndX=-20 EndY=200 EndZ=0
    g31: LineSegment [constr] StartX=-20 StartY=200 StartZ=0 EndX=-20 EndY=100 EndZ=0
    g32: LineSegment [constr] StartX=25 StartY=100 StartZ=0 EndX=20 EndY=100 EndZ=0
    g33: LineSegment [constr] StartX=20 StartY=100 StartZ=0 EndX=20 EndY=200 EndZ=0
    g34: LineSegment [constr] StartX=20 StartY=200 StartZ=0 EndX=20 EndY=300 EndZ=0
    g35: Circle CenterX=-20 CenterY=300 CenterZ=0 NormalX=0 NormalY=0 NormalZ=1 AngleXU=0 Radius=1.5
    g36: Circle CenterX=20 CenterY=300 CenterZ=0 NormalX=0 NormalY=0 NormalZ=1 AngleXU=0 Radius=1.5
    g37: Circle CenterX=-20 CenterY=200 CenterZ=0 NormalX=0 NormalY=0 NormalZ=1 AngleXU=0 Radius=1.5
    g38: Circle CenterX=20 CenterY=200 CenterZ=0 NormalX=0 NormalY=0 NormalZ=1 AngleXU=0 Radius=1.5
    g39: Circle CenterX=-20 CenterY=100 CenterZ=0 NormalX=0 NormalY=0 NormalZ=1 AngleXU=0 Radius=1.5
    g40: Circle CenterX=20 CenterY=100 CenterZ=0 NormalX=0 NormalY=0 NormalZ=1 AngleXU=0 Radius=1.5
  constraints (85):
    c: Diameter(g0) = 28
    c: Coincident(g1,g0)
    c: Vertical(g1)
    c: Coincident(g2,g1)
    c: Diameter(g3) = 10
    c: Diameter(g4) = 4
    c: Coincident(g4,g1)
    c: Diameter(g5) = 4
    c: Coincident(g5,g0)
    c: Diameter(g6) = 22
    c: Tangent(g7,g9) = 1.5708
    c: Tangent(g7,g10) = -1.5708
    c: Tangent(g8,g9) = 1.5708
    c: Tangent(g8,g10) = -1.5708
    c: Equal(g7,g8)
    c: Radius(g7) = 25
    c: Coincident(g7,g3)
    c: Coincident(g8,g1)
    c: Vertical(g9)
    c: Diameter(g12) = 2.5
    c: Diameter(g13) = 2.5
    c: Diameter(g14) = 2.5
    c: Diameter(g11) = 2.5
    c: Diameter(g16) = 2.5
    c: Diameter(g17) = 2.5
    c: Diameter(g18) = 2.5
    c: Diameter(g15) = 2.5
    c: Symmetric(g10,g10,g19)
    c: Symmetric(g9,g9,g19)
    c: Distance(g20) = 30
    c: Horizontal(g20)
    c: Coincident(g20,g19)
    c: Distance(g21) = 30
    c: Horizontal(g21)
    c: Coincident(g21,g7)
    c: PointOnObject(g21,g-1)
    c: Distance(g22) = 30
    c: Horizontal(g22)
    c: Coincident(g22,g8)
    c: Coincident(g23,g20)
    c: Coincident(g23,g22)
    c: Coincident(g24,g20)
    c: Coincident(g24,g21)
    c: Symmetric(g24,g24,g25)
    c: PointOnObject(g25,g10)
    c: Horizontal(g25)
    c: Coincident(g26,g25)
    c: PointOnObject(g26,g9)
    c: Horizontal(g26)
    c: Symmetric(g23,g23,g27)
    c: PointOnObject(g27,g10)
    c: Horizontal(g27)
    c: Coincident(g28,g27)
    c: PointOnObject(g28,g9)
    c: Horizontal(g28)
    c: Distance(g29) = 5
    c: Horizontal(g29)
    c: Coincident(g29,g28)
    c: Coincident(g30,g29)
    c: PointOnObject(g30,g19)
    c: Vertical(g30)
    c: Coincident(g31,g30)
    c: PointOnObject(g31,g26)
    c: Vertical(g31)
    c: Distance(g32) = 5
    c: Horizontal(g32)
    c: Coincident(g32,g25)
    c: Coincident(g33,g32)
    c: PointOnObject(g33,g19)
    c: Vertical(g33)
    c: Coincident(g34,g33)
    c: PointOnObject(g34,g28)
    c: Vertical(g34)
    c: Diameter(g35) = 3
    c: Coincident(g35,g29)
    c: Coincident(g36,g34)
    c: Equal(g35,g36)
    c: Coincident(g37,g30)
    c: Equal(g35,g37)
    c: Coincident(g38,g33)
    c: Equal(g37,g38)
    c: Coincident(g39,g31)
    c: Equal(g37,g39)
    c: Coincident(g40,g32)
    c: Equal(g39,g40)
FEATURE [PartDesign::Pad] Pad003
  Direction = (0,0,1)
  Length = 4
  Length2 = 10
  Profile = -> Sketch003
  ReferenceAxis = -> Sketch003 [N_Axis]
  Refine = true
  Suppressed = false
  Type = 0
FEATURE [PartDesign::Body] Body005  label="arm_high_002"
  AllowCompound = false
  Group = -> [Sketch003,Pad003]
  Origin = -> Origin005
  Placement = pos=(387.832,472.58,105.3) rot=(0,0,1;1.75335rad)
  Tip = -> Pad003
FEATURE [App::FeaturePython] Joint007  label="Fixed002"  # Assembly joint (typed FeaturePython)
  Activated = true
  AngleMax = 0
  AngleMin = 0
  Detach1 = false
  Detach2 = false
  Distance = 0
  Distance2 = 0
  EnableAngleMax = false
  EnableAngleMin = false
  EnableLengthMax = false
  EnableLengthMin = false
  JointType = 0 (Fixed)
  LengthMax = 0
  LengthMin = 0
  Offset2 = pos=(0,0,80) rot=(0,0,1;0rad)
  Placement2 = pos=(0,0,84) rot=(0,0,1;0rad)
  Reference1 = -> Assembly [Body004.Edge32,Body004.Edge32]
  Reference2 = -> Assembly [Body.Edge33,Body.Edge33]
FEATURE [App::FeaturePython] Joint008  label="Fixed003"  # Assembly joint (typed FeaturePython)
  Activated = true
  AngleMax = 0
  AngleMin = 0
  Detach1 = false
  Detach2 = false
  Distance = 0
  Distance2 = 0
  EnableAngleMax = false
  EnableAngleMin = false
  EnableLengthMax = false
  EnableLengthMin = false
  JointType = 0 (Fixed)
  LengthMax = 0
  LengthMin = 0
  Offset2 = pos=(0,0,72) rot=(0,0,1;0rad)
  Placement1 = pos=(5.68e-14,400.001,0) rot=(0,0,1;0rad)
  Placement2 = pos=(5.68e-14,400.001,76) rot=(0,0,1;0rad)
  Reference1 = -> Assembly [Body005.Edge17,Body005.Edge17]
  Reference2 = -> Assembly [Body001.Edge18,Body001.Edge18]
FEATURE [App::Link] Body006
  LinkPlacement = pos=(-5.52126,399.962,92.3) rot=(0,0,1;1.75335rad)
  LinkedObject = -> <external pulleys/gt2_48T_pulley_double.FCStd>#Body
  Placement = pos=(-5.52126,399.962,92.3) rot=(0,0,1;1.75335rad)
FEATURE [App::FeaturePython] Joint009  label="Revolute002"  # Assembly joint (typed FeaturePython)
  Activated = true
  AngleMax = 0
  AngleMin = 0
  Detach1 = false
  Detach2 = false
  Distance = 0
  Distance2 = 0
  EnableAngleMax = false
  EnableAngleMin = false
  EnableLengthMax = false
  EnableLengthMin = false
  JointType = 1 (Revolute)
  LengthMax = 0
  LengthMin = 0
  Offset2 = pos=(0,0,-3) rot=(0,0,1;0rad)
  Placement1 = pos=(0,0,10) rot=(1,0,0;3.14159rad)
  Placement2 = pos=(5.68e-14,400.001,-3) rot=(0,0,1;0rad)
  Reference1 = -> Assembly [Body006.Edge875,Body006.Edge875]
  Reference2 = -> Assembly [Body005.Edge17,Body005.Edge17]
FEATURE [App::Link] DC05_M01_DUMMY002
  LinkPlacement = pos=(0,0,138) rot=(0,1,0;3.14159rad)
  LinkedObject = -> <external srv.FCStd>#Part__Feature
  Placement = pos=(0,0,138) rot=(0,1,0;3.14159rad)
FEATURE [App::FeaturePython] Joint010  label="Fixed004"  # Assembly joint (typed FeaturePython)
  Activated = true
  AngleMax = 0
  AngleMin = 0
  Detach1 = false
  Detach2 = false
  Distance = 0
  Distance2 = 0
  EnableAngleMax = false
  EnableAngleMin = false
  EnableLengthMax = false
  EnableLengthMin = false
  JointType = 0 (Fixed)
  LengthMax = 0
  LengthMin = 0
  Offset2 = pos=(0,0,82) rot=(0,0,1;0rad)
  Placement1 = pos=(0,0,28) rot=(-0.707107,-0.707107,0;3.14159rad)
  Placement2 = pos=(0,0,110) rot=(0,0,1;1.5708rad)
  Reference1 = -> Assembly [DC05_M01_DUMMY002.Edge912,DC05_M01_DUMMY002.Edge912]
  Reference2 = -> Assembly [DC05_M01_DUMMY.Edge915,DC05_M01_DUMMY.Edge915]
FEATURE [App::Link] DC05_M01_DUMMY003
  LinkPlacement = pos=(-0.487674,37.9968,130.05) rot=(0.999976,0.006902,0;3.14159rad)
  LinkedObject = -> <external srv.FCStd>#Part__Feature
  Placement = pos=(-0.487674,37.9968,130.05) rot=(0.999976,0.006902,0;3.14159rad)
FEATURE [App::FeaturePython] Joint011  label="Fixed005"  # Assembly joint (typed FeaturePython)
  Activated = true
  AngleMax = 0
  AngleMin = 0
  Detach1 = false
  Detach2 = false
  Distance = 0
  Distance2 = 0
  EnableAngleMax = false
  EnableAngleMin = false
  EnableLengthMax = false
  EnableLengthMin = false
  JointType = 0 (Fixed)
  LengthMax = 0
  LengthMin = 0
  Offset2 = pos=(0,0,-65) rot=(0,0,1;0rad)
  Placement1 = pos=(0,0,28) rot=(0,0,1;1.5708rad)
  Placement2 = pos=(0,0,93) rot=(-0.707107,-0.707107,0;3.14159rad)
  Reference1 = -> Assembly [DC05_M01_DUMMY003.Edge915,DC05_M01_DUMMY003.Edge915]
  Reference2 = -> Assembly [DC05_M01_DUMMY001.Edge912,DC05_M01_DUMMY001.Edge912]
FEATURE [App::Link] Body007
  LinkPlacement = pos=(-0.487674,37.9968,100.55) rot=(0.71197,-0.70221,0;3.14159rad)
  LinkedObject = -> <external pulleys/gt2_24T_pulley_open.FCStd>#Body
  Placement = pos=(-0.487674,37.9968,100.55) rot=(0.71197,-0.70221,0;3.14159rad)
FEATURE [App::FeaturePython] Joint012  label="Revolute003"  # Assembly joint (typed FeaturePython)
  Activated = true
  AngleMax = 0
  AngleMin = 0
  Detach1 = false
  Detach2 = false
  Distance = 0
  Distance2 = 0
  EnableAngleMax = false
  EnableAngleMin = false
  EnableLengthMax = false
  EnableLengthMin = false
  JointType = 1 (Revolute)
  LengthMax = 0
  LengthMin = 0
  Placement1 = pos=(0,0,-6) rot=(-1,0,0;3.14159rad)
  Placement2 = pos=(0,0,23.5) rot=(0,0,1;1.5708rad)
  Reference1 = -> Assembly [Body007.Edge529,Body007.Edge529]
  Reference2 = -> Assembly [DC05_M01_DUMMY003.Edge889,DC05_M01_DUMMY003.Edge889]
FEATURE [Assembly::JointGroup] Joints
  Group = -> [GroundedJoint,Joint,Joint001,Joint002,Joint003,Joint004,Joint005,Joint006,Joint007,Joint008,Joint009,Joint010,Joint011,Joint012]
FEATURE [Assembly::AssemblyObject] Assembly
  Group = -> [Joints,Body,Body004,Body001,Body005,DC05_M01_DUMMY,GroundedJoint,Joint,Joint001,DC05_M01_DUMMY001,Joint002,Joint003,Joint004,Body002,Joint005,Body003,Joint006,Joint007,Joint008,Body006,Joint009,DC05_M01_DUMMY002,Joint010,DC05_M01_DUMMY003,Joint011,Body007,Joint012]
  Origin = -> Origin003
  Type = Assembly

RESOLVED EXTERNAL PARTS (link-assembly join: the EXTERNAL_REF files above that resolve inside this repo's crawl, each included once):
---- part pulleys/gt2_24T_pulley_open.FCStd = doc fcstd_ee15d791d3af ----
FCSTD DOCUMENT  (FreeCAD 1.0R39109 (Git))
Label: gt2_24T_pulley_open
License: All rights reserved
LicenseURL: https://en.wikipedia.org/wiki/All_rights_reserved
objects: Sketcher::SketchObject×8, PartDesign::Chamfer×7, PartDesign::Pad×4, PartDesign::Pocket×4, PartDesign::Body×2, Part::FeaturePython×1, PartDesign::FeatureBase×1, PartDesign::ShapeBinder×1, App::Part×1
note: 67 computed .brp shape members not serialized (recipe doc carries the construction recipe); baked Part::Feature solids carry a one-line shape summary decoded from their .brp

FEATURE [Part::FeaturePython] TimingGear  # WARN: FeaturePython — macro-defined, semantics opaque (R4)
  AttacherType = Attacher::AttachEngine3D
  h = 0.75
  height = 8
  num_teeth = 24
  offset = 0.4
  pitch = 2
  r0 = 0.555
  r1 = 1
  rs = 0.15
  type = 0
  u = 0.254
  version = 1.3.0
FEATURE [PartDesign::FeatureBase] BaseFeature
  BaseFeature = -> TimingGear
  Suppressed = false
FEATURE [Sketcher::SketchObject] Sketch
  ArcFitTolerance = 1e-06
  AttachmentSupport = -> [BaseFeature]
  FullyConstrained = true
  MakeInternals = false
  MapMode = 5
  Placement = pos=(0,0,0) rot=(1,0,0;3.14159rad)
  sketch-geometry (1):
    g0: Circle CenterX=0 CenterY=0 CenterZ=0 NormalX=0 NormalY=0 NormalZ=1 AngleXU=0 Radius=9
  constraints (2):
    c: Diameter(g0) = 18
    c: Coincident(g0,g-1)
FEATURE [PartDesign::Pad] Pad
  BaseFeature = -> BaseFeature
  Direction = (0,0,-1)
  Length = 2
  Length2 = 10
  Profile = -> Sketch
  ReferenceAxis = -> Sketch [N_Axis]
  Refine = true
  Suppressed = false
  Type = 0
FEATURE [Sketcher::SketchObject] Sketch001
  ArcFitTolerance = 1e-06
  AttachmentSupport = -> [Pad]
  FullyConstrained = true
  MakeInternals = false
  MapMode = 5
  Placement = pos=(0,0,-2) rot=(1,0,0;3.14159rad)
  sketch-geometry (1):
    g0: Circle CenterX=0 CenterY=0 CenterZ=0 NormalX=0 NormalY=0 NormalZ=1 AngleXU=0 Radius=14
  constraints (2):
    c: Diameter(g0) = 28
    c: Coincident(g0,g-1)
FEATURE [PartDesign::Pad] Pad001
  BaseFeature = -> Pad
  Direction = (0,0,-1)
  Length = 3
  Length2 = 10
  Profile = -> Sketch001
  ReferenceAxis = -> Sketch001 [N_Axis]
  Refine = true
  Suppressed = false
  Type = 0
FEATURE [Sketcher::SketchObject] Sketch002
  ArcFitTolerance = 1e-06
  AttachmentSupport = -> [Pad001]
  FullyConstrained = false
  MakeInternals = false
  MapMode = 5
  Placement = pos=(0,0,-5) rot=(1,0,0;3.14159rad)
  sketch-geometry (7):
    g0: Circle [constr] CenterX=0 CenterY=5.078e-13 CenterZ=0 NormalX=0 NormalY=0 NormalZ=1 AngleXU=0 Radius=11
    g1: LineSegment [constr] StartX=0 StartY=5.078e-13 StartZ=0 EndX=0 EndY=11 EndZ=0
    g2: Circle CenterX=0 CenterY=11 CenterZ=0 NormalX=0 NormalY=0 NormalZ=1 AngleXU=0 Radius=5.092e-13
    g3: Circle CenterX=0 CenterY=11 CenterZ=0 NormalX=0 NormalY=0 NormalZ=1 AngleXU=0 Radius=1.25
    g4: Circle CenterX=-11 CenterY=0 CenterZ=0 NormalX=0 NormalY=0 NormalZ=1 AngleXU=0 Radius=1.25
    g5: Circle CenterX=0 CenterY=-11 CenterZ=0 NormalX=0 NormalY=0 NormalZ=1 AngleXU=0 Radius=1.25
    g6: Circle CenterX=11 CenterY=0 CenterZ=0 NormalX=0 NormalY=0 NormalZ=1 AngleXU=0 Radius=1.25
  constraints (12):
    c: Diameter(g0) = 22
    c: Coincident(g0,g-1)
    c: Coincident(g1,g0)
    c: PointOnObject(g1,g0)
    c: Vertical(g1)
    c: Coincident(g2,g1)
    c: Tangent(g2,g0)
    c: Coincident(g3,g1)
    c: Diameter(g3) = 2.5
    c: Diameter(g4) = 2.5
    c: Diameter(g5) = 2.5
    c: Diameter(g6) = 2.5
FEATURE [PartDesign::Pocket] Pocket
  BaseFeature = -> Pad001
  Direction = (0,0,1)
  Length = 19
  Length2 = 5
  Profile = -> Sketch002
  ReferenceAxis = -> Sketch002 [N_Axis]
  Refine = true
  Suppressed = false
  Type = 0
FEATURE [Sketcher::SketchObject] Sketch003
  ArcFitTolerance = 1e-06
  AttachmentSupport = -> [Pocket]
  FullyConstrained = true
  MakeInternals = false
  MapMode = 5
  Placement = pos=(0,0,-5) rot=(1,0,0;3.14159rad)
  sketch-geometry (1):
    g0: Circle CenterX=0 CenterY=0 CenterZ=0 NormalX=0 NormalY=0 NormalZ=1 AngleXU=0 Radius=6
  constraints (2):
    c: Coincident(g0,g-1)
    c: Diameter(g0) = 12
FEATURE [PartDesign::Pocket] Pocket001
  BaseFeature = -> Pocket
  Direction = (0,0,1)
  Length = 5
  Length2 = 5
  Profile = -> Sketch003
  ReferenceAxis = -> Sketch003 [N_Axis]
  Refine = true
  Suppressed = false
  Type = 0
FEATURE [Sketcher::SketchObject] Sketch004
  ArcFitTolerance = 1e-06
  AttachmentSupport = -> [Pocket001]
  FullyConstrained = true
  MakeInternals = false
  MapMode = 5
  Placement = pos=(0,0,-9e-16) rot=(1,0,0;3.14159rad)
  sketch-geometry (1):
    g0: Circle CenterX=0 CenterY=0 CenterZ=0 NormalX=0 NormalY=0 NormalZ=1 AngleXU=0 Radius=1.75
  constraints (2):
    c: Coincident(g0,g-1)
    c: Diameter(g0) = 3.5
FEATURE [PartDesign::Pocket] Pocket002
  BaseFeature = -> Pocket001
  Direction = (0,0,1)
  Length = 20
  Length2 = 5
  Profile = -> Sketch004
  ReferenceAxis = -> Sketch004 [N_Axis]
  Refine = true
  Suppressed = false
  Type = 0
FEATURE [PartDesign::Chamfer] Chamfer
  Angle = 45
  Base = -> Pocket002 [Edge437]
  BaseFeature = -> Pocket002
  ChamferType = 0
  FlipDirection = false
  Refine = true
  Size = 4.2
  Size2 = 1
  SupportTransform = false
  Suppressed = false
  UseAllEdges = false
FEATURE [PartDesign::Chamfer] Chamfer001
  Angle = 45
  Base = -> Chamfer [Edge441]
  BaseFeature = -> Chamfer
  ChamferType = 0
  FlipDirection = false
  Refine = true
  Size = 0.5
  Size2 = 1
  SupportTransform = false
  Suppressed = false
  UseAllEdges = false
FEATURE [PartDesign::Chamfer] Chamfer002
  Angle = 45
  Base = -> Chamfer001 [Edge439,Edge447]
  BaseFeature = -> Chamfer001
  ChamferType = 0
  FlipDirection = false
  Refine = true
  Size = 0.5
  Size2 = 1
  SupportTransform = false
  Suppressed = false
  UseAllEdges = false
FEATURE [PartDesign::Chamfer] Chamfer003
  Angle = 45
  Base = -> Chamfer002 [Edge22,Edge15,Edge17,Edge15,Edge9,Edge11]
  BaseFeature = -> Chamfer002
  ChamferType = 0
  FlipDirection = false
  Refine = true
  Size = 0.5
  Size2 = 1
  SupportTransform = false
  Suppressed = false
  UseAllEdges = false
FEATURE [PartDesign::Chamfer] Chamfer004
  Angle = 45
  Base = -> Chamfer003 [Edge473]
  BaseFeature = -> Chamfer003
  ChamferType = 0
  FlipDirection = false
  Refine = true
  Size = 0.5
  Size2 = 1
  SupportTransform = false
  Suppressed = false
  UseAllEdges = false
FEATURE [PartDesign::ShapeBinder] CopyChamfer004
  TraceSupport = false
FEATURE [Sketcher::SketchObject] Sketch005
  ArcFitTolerance = 1e-06
  AttachmentSupport = -> [CopyChamfer004]
  FullyConstrained = true
  MakeInternals = false
  MapMode = 5
  Placement = pos=(0,0,8) rot=(0,0,1;0rad)
  sketch-geometry (1):
    g0: Circle CenterX=0 CenterY=0 CenterZ=0 NormalX=0 NormalY=0 NormalZ=1 AngleXU=0 Radius=11
  constraints (2):
    c: Diameter(g0) = 22
    c: Coincident(g0,g-1)
FEATURE [PartDesign::Pad] Pad002
  Direction = (0,0,1)
  Length = 2
  Length2 = 10
  Profile = -> Sketch005
  ReferenceAxis = -> Sketch005 [N_Axis]
  Refine = true
  Suppressed = false
  Type = 0
FEATURE [Sketcher::SketchObject] Sketch006
  ArcFitTolerance = 1e-06
  AttachmentSupport = -> [Pad002]
  FullyConstrained = true
  MakeInternals = false
  MapMode = 5
  Placement = pos=(0,0,10) rot=(0,0,1;0rad)
  sketch-geometry (1):
    g0: Circle CenterX=0 CenterY=0 CenterZ=0 NormalX=0 NormalY=0 NormalZ=1 AngleXU=0 Radius=1.5
  constraints (2):
    c: Diameter(g0) = 3
    c: Coincident(g0,g-1)
FEATURE [PartDesign::Pocket] Pocket003
  BaseFeature = -> Pad002
  Direction = (0,0,-1)
  Length = 15
  Length2 = 5
  Profile = -> Sketch006
  ReferenceAxis = -> Sketch006 [N_Axis]
  Refine = true
  Suppressed = false
  Type = 0
FEATURE [PartDesign::Chamfer] Chamfer005
  Angle = 45
  Base = -> Pocket003 [Edge2,Edge3,Edge5,Edge4]
  BaseFeature = -> Pocket003
  ChamferType = 0
  FlipDirection = false
  Refine = true
  Size = 0.5
  Size2 = 1
  SupportTransform = false
  Suppressed = false
  UseAllEdges = false
FEATURE [PartDesign::Body] Body001
  AllowCompound = false
  Group = -> [CopyChamfer004,Sketch005,Pad002,Sketch006,Pocket003,Chamfer005]
  Origin = -> Origin001
  Tip = -> Chamfer005
FEATURE [Sketcher::SketchObject] Sketch007
  ArcFitTolerance = 1e-06
  AttachmentSupport = -> [Chamfer004]
  ExternalGeometry = -> [Chamfer004]
  FullyConstrained = true
  MakeInternals = false
  MapMode = 5
  Placement = pos=(0,0,-2) rot=(0,0,1;0rad)
  sketch-geometry (25):
    g0: Circle [constr] CenterX=0 CenterY=0 CenterZ=0 NormalX=0 NormalY=0 NormalZ=1 AngleXU=0 Radius=9
    g1: LineSegment [constr] StartX=0 StartY=0 StartZ=0 EndX=7.79423 EndY=-4.5 EndZ=0
    g2: LineSegment [constr] StartX=0 StartY=0 StartZ=0 EndX=4.5 EndY=-7.79423 EndZ=0
    g3: LineSegment StartX=7.79423 StartY=-4.5 StartZ=0 EndX=11.6913 EndY=-6.75 EndZ=0
    g4: LineSegment StartX=4.5 StartY=-7.79423 StartZ=0 EndX=6.75 EndY=-11.6913 EndZ=0
    g5: LineSegment [constr] StartX=0 StartY=0 StartZ=0 EndX=7.79423 EndY=4.5 EndZ=0
    g6: LineSegment [constr] StartX=0 StartY=0 StartZ=0 EndX=4.5 EndY=7.79423 EndZ=0
    g7: LineSegment [constr] StartX=0 StartY=0 StartZ=0 EndX=-4.5 EndY=7.79423 EndZ=0
    g8: LineSegment [constr] StartX=0 StartY=0 StartZ=0 EndX=-7.79423 EndY=4.5 EndZ=0
    g9: LineSegment [constr] StartX=0 StartY=0 StartZ=0 EndX=-7.79423 EndY=-4.5 EndZ=0
    g10: LineSegment [constr] StartX=0 StartY=0 StartZ=0 EndX=-4.5 EndY=-7.79423 EndZ=0
    g11: LineSegment StartX=7.79423 StartY=4.5 StartZ=0 EndX=11.6913 EndY=6.75 EndZ=0
    g12: LineSegment StartX=4.5 StartY=7.79423 StartZ=0 EndX=6.75 EndY=11.6913 EndZ=0
    g13: LineSegment StartX=-4.5 StartY=7.79423 StartZ=0 EndX=-6.75 EndY=11.6913 EndZ=0
    g14: LineSegment StartX=-7.79423 StartY=4.5 StartZ=0 EndX=-11.6913 EndY=6.75 EndZ=0
    g15: LineSegment StartX=-7.79423 StartY=-4.5 StartZ=0 EndX=-11.6913 EndY=-6.75 EndZ=0
    g16: LineSegment StartX=-4.5 StartY=-7.79423 StartZ=0 EndX=-6.75 EndY=-11.6913 EndZ=0
    g17: ArcOfCircle CenterX=0 CenterY=0 CenterZ=0 NormalX=0 NormalY=0 NormalZ=1 AngleXU=0 Radius=9 StartAngle=0.523599 EndAngle=1.0472
    g18: ArcOfCircle CenterX=0 CenterY=0 CenterZ=0 NormalX=0 NormalY=0 NormalZ=1 AngleXU=0 Radius=9 StartAngle=2.0944 EndAngle=2.61799
    g19: ArcOfCircle CenterX=0 CenterY=0 CenterZ=0 NormalX=0 NormalY=0 NormalZ=1 AngleXU=0 Radius=9 StartAngle=3.66519 EndAngle=4.18879
    g20: ArcOfCircle CenterX=0 CenterY=0 CenterZ=0 NormalX=0 NormalY=0 NormalZ=1 AngleXU=0 Radius=9 StartAngle=5.23599 EndAngle=5.75959
    g21: ArcOfCircle CenterX=0 CenterY=0 CenterZ=0 NormalX=0 NormalY=0 NormalZ=1 AngleXU=0 Radius=13.5 StartAngle=0.523599 EndAngle=1.0472
    g22: ArcOfCircle CenterX=0 CenterY=0 CenterZ=0 NormalX=0 NormalY=0 NormalZ=1 AngleXU=0 Radius=13.5 StartAngle=2.0944 EndAngle=2.61799
    g23: ArcOfCircle CenterX=0 CenterY=0 CenterZ=0 NormalX=0 NormalY=0 NormalZ=1 AngleXU=0 Radius=13.5 StartAngle=3.66519 EndAngle=4.18879
    g24: ArcOfCircle CenterX=0 CenterY=0 CenterZ=0 NormalX=0 NormalY=0 NormalZ=1 AngleXU=0 Radius=13.5 StartAngle=5.23599 EndAngle=5.75959
  constraints (80):
    c: Coincident(g0,g-1)
    c: Diameter(g0) = 18
    c: Coincident(g1,g0)
    c: PointOnObject(g1,g0)
    c: Angle(g1,g-1) = 0.523599
    c: Coincident(g2,g0)
    c: PointOnObject(g2,g0)
    c: Angle(g2,g1) = 0.523599
    c: Coincident(g3,g1)
    c: PointOnObject(g3,g-4)
    c: Parallel(g1,g3)
    c: Coincident(g4,g2)
    c: PointOnObject(g4,g-4)
    c: Parallel(g2,g4)
    c: Coincident(g5,g0)
    c: PointOnObject(g5,g0)
    c: Coincident(g6,g0)
    c: PointOnObject(g6,g0)
    c: Coincident(g7,g0)
    c: PointOnObject(g7,g0)
    c: Coincident(g8,g0)
    c: PointOnObject(g8,g0)
    c: Coincident(g9,g0)
    c: PointOnObject(g9,g0)
    c: Coincident(g10,g0)
    c: PointOnObject(g10,g0)
    c: Angle(g-1,g5) = 0.523599
    c: Angle(g5,g6) = 0.523599
    c: Angle(g6,g7) = 1.0472
    c: Angle(g7,g8) = 0.523599
    c: Angle(g8,g9) = 1.0472
    c: Angle(g9,g10) = 0.523599
    c: Coincident(g11,g5)
    c: PointOnObject(g11,g-4)
    c: Coincident(g12,g6)
    c: PointOnObject(g12,g-4)
    c: Coincident(g13,g7)
    c: PointOnObject(g13,g-4)
    c: Coincident(g14,g8)
    c: PointOnObject(g14,g-4)
    c: Coincident(g15,g9)
    c: PointOnObject(g15,g-4)
    c: Coincident(g16,g10)
    c: PointOnObject(g16,g-4)
    c: Parallel(g5,g11)
    c: Parallel(g6,g12)
    c: Parallel(g7,g13)
    c: Parallel(g8,g14)
    c: Parallel(g9,g15)
    c: Parallel(g10,g16)
    c: Coincident(g17,g0)
    c: Coincident(g20,g1)
    c: PointOnObject(g17,g5)
    c: Equal(g17,g18)
    c: PointOnObject(g17,g6)
    c: PointOnObject(g18,g7)
    c: Coincident(g17,g18)
    c: Equal(g18,g19)
    c: PointOnObject(g18,g8)
    c: PointOnObject(g19,g9)
    c: Coincident(g18,g19)
    c: Equal(g19,g20)
    c: PointOnObject(g19,g10)
    c: PointOnObject(g20,g2)
    c: Coincident(g19,g20)
    c: Coincident(g21,g0)
    c: Coincident(g21,g11)
    c: PointOnObject(g24,g3)
    c: Equal(g21,g22)
    c: PointOnObject(g21,g12)
    c: PointOnObject(g22,g13)
    c: Coincident(g21,g22)
    c: Equal(g22,g23)
    c: PointOnObject(g22,g14)
    c: PointOnObject(g23,g15)
    c: Coincident(g22,g23)
    c: Equal(g23,g24)
    c: PointOnObject(g23,g16)
    c: PointOnObject(g24,g4)
    c: Coincident(g23,g24)
FEATURE [PartDesign::Pad] Pad003
  BaseFeature = -> Chamfer004
  Direction = (0,0,1)
  Length = 1.5
  Length2 = 10
  Profile = -> Sketch007
  ReferenceAxis = -> Sketch007 [N_Axis]
  Refine = true
  Suppressed = false
  Type = 0
FEATURE [PartDesign::Chamfer] Chamfer006
  Angle = 45
  Base = -> Pad003 [Edge453,Edge471,Edge465,Edge459]
  BaseFeature = -> Pad003
  ChamferType = 1
  FlipDirection = false
  Refine = true
  Size = 4.4
  Size2 = 1.4
  SupportTransform = false
  Suppressed = false
  UseAllEdges = false
FEATURE [PartDesign::Body] Body
  AllowCompound = false
  BaseFeature = -> TimingGear
  Group = -> [BaseFeature,Sketch,Pad,Sketch001,Pad001,Sketch002,Pocket,Sketch003,Pocket001,Sketch004,Pocket002,Chamfer,Chamfer001,Chamfer002,Chamfer003,Chamfer004,Sketch007,Pad003,Chamfer006]
  Origin = -> Origin
  Tip = -> Chamfer006
FEATURE [App::Part] Part
  Group = -> [TimingGear,Body,Body001]
  Origin = -> Origin002
---- part pulleys/gt2_48T_pulley.FCStd = doc fcstd_034fdf5fdbef ----
FCSTD DOCUMENT  (FreeCAD 1.0R39109 (Git))
Label: gt2_48T_pulley
License: All rights reserved
LicenseURL: https://en.wikipedia.org/wiki/All_rights_reserved
objects: Sketcher::SketchObject×6, PartDesign::Chamfer×5, PartDesign::Pocket×4, PartDesign::Pad×2, Part::FeaturePython×1, PartDesign::FeatureBase×1, PartDesign::Body×1
note: 49 computed .brp shape members not serialized (recipe doc carries the construction recipe); baked Part::Feature solids carry a one-line shape summary decoded from their .brp

FEATURE [Part::FeaturePython] TimingGear  # WARN: FeaturePython — macro-defined, semantics opaque (R4)
  AttacherType = Attacher::AttachEngine3D
  h = 0.75
  height = 8
  num_teeth = 48
  offset = 0.4
  pitch = 2
  r0 = 0.555
  r1 = 1
  rs = 0.15
  type = 0
  u = 0.254
  version = 1.3.0
FEATURE [PartDesign::FeatureBase] BaseFeature
  BaseFeature = -> TimingGear
  Suppressed = false
FEATURE [Sketcher::SketchObject] Sketch
  ArcFitTolerance = 1e-06
  AttachmentSupport = -> [BaseFeature]
  FullyConstrained = true
  MakeInternals = false
  MapMode = 5
  Placement = pos=(0,0,0) rot=(1,0,0;3.14159rad)
  sketch-geometry (1):
    g0: Circle CenterX=0 CenterY=0 CenterZ=0 NormalX=0 NormalY=0 NormalZ=1 AngleXU=0 Radius=19
  constraints (2):
    c: Diameter(g0) = 38
    c: Coincident(g0,g-1)
FEATURE [PartDesign::Pad] Pad
  BaseFeature = -> BaseFeature
  Direction = (0,0,-1)
  Length = 2
  Length2 = 10
  Profile = -> Sketch
  ReferenceAxis = -> Sketch [N_Axis]
  Refine = true
  Suppressed = false
  Type = 0
FEATURE [Sketcher::SketchObject] Sketch001
  ArcFitTolerance = 1e-06
  AttachmentSupport = -> [Pad]
  FullyConstrained = false
  MakeInternals = false
  MapMode = 5
  Placement = pos=(0,0,-2) rot=(1,0,0;3.14159rad)
  sketch-geometry (6):
    g0: Circle [constr] CenterX=0 CenterY=0 CenterZ=0 NormalX=0 NormalY=0 NormalZ=1 AngleXU=0 Radius=11
    g1: LineSegment [constr] StartX=0 StartY=0 StartZ=0 EndX=0 EndY=11 EndZ=0
    g2: Circle CenterX=0 CenterY=11 CenterZ=0 NormalX=0 NormalY=0 NormalZ=1 AngleXU=0 Radius=1.5
    g3: Circle CenterX=-11 CenterY=0 CenterZ=0 NormalX=0 NormalY=0 NormalZ=1 AngleXU=0 Radius=1.5
    g4: Circle CenterX=0 CenterY=-11 CenterZ=0 NormalX=0 NormalY=0 NormalZ=1 AngleXU=0 Radius=1.5
    g5: Circle CenterX=11 CenterY=0 CenterZ=0 NormalX=0 NormalY=0 NormalZ=1 AngleXU=0 Radius=1.5
  constraints (10):
    c: Diameter(g0) = 22
    c: Coincident(g0,g-1)
    c: Coincident(g1,g0)
    c: PointOnObject(g1,g0)
    c: Vertical(g1)
    c: Coincident(g2,g1)
    c: Diameter(g2) = 3
    c: Equal(g5,g2)
    c: Equal(g4,g5)
    c: Equal(g3,g4)
FEATURE [Sketcher::SketchObject] Sketch002
  ArcFitTolerance = 1e-06
  AttachmentSupport = -> [Pad]
  ExternalGeometry = -> [Pad]
  FullyConstrained = true
  MakeInternals = false
  MapMode = 5
  Placement = pos=(0,0,8) rot=(0,0,1;0rad)
  sketch-geometry (1):
    g0: Circle CenterX=0 CenterY=0 CenterZ=0 NormalX=0 NormalY=0 NormalZ=1 AngleXU=0 Radius=19
  constraints (2):
    c: Coincident(g0,g-1)
    c: Diameter(g0) = 38
FEATURE [PartDesign::Pad] Pad001
  BaseFeature = -> Pad
  Direction = (0,0,1)
  Length = 2
  Length2 = 10
  Profile = -> Sketch002
  ReferenceAxis = -> Sketch002 [N_Axis]
  Refine = true
  Suppressed = false
  Type = 0
FEATURE [PartDesign::Pocket] Pocket
  BaseFeature = -> Pad001
  Direction = (0,0,1)
  Length = 29
  Length2 = 5
  Profile = -> Sketch001
  ReferenceAxis = -> Sketch001 [N_Axis]
  Refine = true
  Suppressed = false
  Type = 0
FEATURE [Sketcher::SketchObject] Sketch003
  ArcFitTolerance = 1e-06
  AttachmentSupport = -> [Pocket]
  FullyConstrained = true
  MakeInternals = false
  MapMode = 5
  Placement = pos=(0,0,-2) rot=(1,0,0;3.14159rad)
  sketch-geometry (1):
    g0: Circle CenterX=0 CenterY=0 CenterZ=0 NormalX=0 NormalY=0 NormalZ=1 AngleXU=0 Radius=3
  constraints (2):
    c: Diameter(g0) = 6
    c: Coincident(g0,g-1)
FEATURE [PartDesign::Pocket] Pocket001
  BaseFeature = -> Pocket
  Direction = (0,0,1)
  Length = 17
  Length2 = 5
  Profile = -> Sketch003
  ReferenceAxis = -> Sketch003 [N_Axis]
  Refine = true
  Suppressed = false
  Type = 0
FEATURE [PartDesign::Chamfer] Chamfer
  Angle = 45
  Base = -> Pocket001 [Edge11,Edge297,Edge870,Edge586,Edge871,Edge874,Edge875,Edge872]
  BaseFeature = -> Pocket001
  ChamferType = 0
  FlipDirection = false
  Refine = true
  Size = 0.5
  Size2 = 1
  SupportTransform = false
  Suppressed = false
  UseAllEdges = false
FEATURE [Sketcher::SketchObject] Sketch004
  ArcFitTolerance = 1e-06
  AttachmentSupport = -> [Chamfer]
  ExternalGeometry = -> [Chamfer]
  FullyConstrained = false
  MakeInternals = false
  MapMode = 5
  Placement = pos=(0,0,10) rot=(0,0,1;0rad)
  sketch-geometry (28):
    g0: LineSegment StartX=0 StartY=14 StartZ=0 EndX=-2.59808 EndY=12.5 EndZ=0
    g1: LineSegment StartX=-2.59808 StartY=12.5 StartZ=0 EndX=-2.59808 EndY=9.5 EndZ=0
    g2: LineSegment StartX=-2.59808 StartY=9.5 StartZ=0 EndX=-4e-16 EndY=8 EndZ=0
    g3: LineSegment StartX=-4e-16 StartY=8 StartZ=0 EndX=2.59808 EndY=9.5 EndZ=0
    g4: LineSegment StartX=2.59808 StartY=9.5 StartZ=0 EndX=2.59808 EndY=12.5 EndZ=0
    g5: LineSegment StartX=2.59808 StartY=12.5 StartZ=0 EndX=0 EndY=14 EndZ=0
    g6: Circle [constr] CenterX=0 CenterY=11 CenterZ=0 NormalX=0 NormalY=0 NormalZ=1 AngleXU=0 Radius=3
    g7: LineSegment StartX=11 StartY=3 StartZ=0 EndX=8.40192 EndY=1.5 EndZ=0
    g8: LineSegment StartX=8.40192 StartY=1.5 StartZ=0 EndX=8.40192 EndY=-1.5 EndZ=0
    g9: LineSegment StartX=8.40192 StartY=-1.5 StartZ=0 EndX=11 EndY=-3 EndZ=0
    g10: LineSegment StartX=11 StartY=-3 StartZ=0 EndX=13.5981 EndY=-1.5 EndZ=0
    g11: LineSegment StartX=13.5981 StartY=-1.5 StartZ=0 EndX=13.5981 EndY=1.5 EndZ=0
    g12: LineSegment StartX=13.5981 StartY=1.5 StartZ=0 EndX=11 EndY=3 EndZ=0
    g13: Circle [constr] CenterX=11 CenterY=0 CenterZ=0 NormalX=0 NormalY=0 NormalZ=1 AngleXU=0 Radius=3
    g14: LineSegment StartX=0 StartY=-8 StartZ=0 EndX=-2.59808 EndY=-9.5 EndZ=0
    g15: LineSegment StartX=-2.59808 StartY=-9.5 StartZ=0 EndX=-2.59808 EndY=-12.5 EndZ=0
    g16: LineSegment StartX=-2.59808 StartY=-12.5 StartZ=0 EndX=-4e-16 EndY=-14 EndZ=0
    g17: LineSegment StartX=-4e-16 StartY=-14 StartZ=0 EndX=2.59808 EndY=-12.5 EndZ=0
    g18: LineSegment StartX=2.59808 StartY=-12.5 StartZ=0 EndX=2.59808 EndY=-9.5 EndZ=0
    g19: LineSegment StartX=2.59808 StartY=-9.5 StartZ=0 EndX=0 EndY=-8 EndZ=0
    g20: Circle [constr] CenterX=0 CenterY=-11 CenterZ=0 NormalX=0 NormalY=0 NormalZ=1 AngleXU=0 Radius=3
    g21: LineSegment StartX=-11 StartY=3 StartZ=0 EndX=-13.5981 EndY=1.5 EndZ=0
    g22: LineSegment StartX=-13.5981 StartY=1.5 StartZ=0 EndX=-13.5981 EndY=-1.5 EndZ=0
    g23: LineSegment StartX=-13.5981 StartY=-1.5 StartZ=0 EndX=-11 EndY=-3 EndZ=0
    g24: LineSegment StartX=-11 StartY=-3 StartZ=0 EndX=-8.40192 EndY=-1.5 EndZ=0
    g25: LineSegment StartX=-8.40192 StartY=-1.5 StartZ=0 EndX=-8.40192 EndY=1.5 EndZ=0
    g26: LineSegment StartX=-8.40192 StartY=1.5 StartZ=0 EndX=-11 EndY=3 EndZ=0
    g27: Circle [constr] CenterX=-11 CenterY=0 CenterZ=0 NormalX=0 NormalY=0 NormalZ=1 AngleXU=0 Radius=3
  constraints (62):
    c: Coincident(g0,g1)
    c: Coincident(g1,g2)
    c: Coincident(g2,g3)
    c: Coincident(g3,g4)
    c: Coincident(g4,g5)
    c: Coincident(g5,g0)
    c: Equal(g0, g1-g5) x5
    c: PointOnObject(g0,g6)
    c: PointOnObject(g1,g6)
    c: PointOnObject(g2,g6)
    c: PointOnObject(g3,g6)
    c: PointOnObject(g4,g6)
    c: PointOnObject(g5,g6)
    c: Radius(g6) = 3
    c: Coincident(g6,g-3)
    c: PointOnObject(g5,g-2)
    c: Coincident(g7,g8)
    c: Coincident(g8,g9)
    c: Coincident(g9,g10)
    c: Coincident(g10,g11)
    c: Coincident(g11,g12)
    c: Coincident(g12,g7)
    c: Equal(g7, g8-g12) x5
    c: PointOnObject(g7,g13)
    c: PointOnObject(g8,g13)
    c: PointOnObject(g9,g13)
    c: PointOnObject(g10,g13)
    c: PointOnObject(g11,g13)
    c: PointOnObject(g12,g13)
    c: Radius(g13) = 3
    c: Coincident(g13,g-5)
    c: Coincident(g14,g15)
    c: Coincident(g15,g16)
    c: Coincident(g16,g17)
    c: Coincident(g17,g18)
    c: Coincident(g18,g19)
    c: Coincident(g19,g14)
    c: Equal(g14, g15-g19) x5
    c: PointOnObject(g14,g20)
    c: PointOnObject(g15,g20)
    c: PointOnObject(g16,g20)
    c: PointOnObject(g17,g20)
    c: PointOnObject(g18,g20)
    c: PointOnObject(g19,g20)
    c: Radius(g20) = 3
    c: Coincident(g20,g-6)
    c: PointOnObject(g19,g-2)
    c: Coincident(g21,g22)
    c: Coincident(g22,g23)
    c: Coincident(g23,g24)
    c: Coincident(g24,g25)
    c: Coincident(g25,g26)
    c: Coincident(g26,g21)
    c: Equal(g21, g22-g26) x5
    c: PointOnObject(g21,g27)
    c: PointOnObject(g22,g27)
    c: PointOnObject(g23,g27)
    c: PointOnObject(g24,g27)
    c: PointOnObject(g25,g27)
    c: PointOnObject(g26,g27)
    c: Radius(g27) = 3
    c: Coincident(g27,g-4)
FEATURE [PartDesign::Pocket] Pocket002
  BaseFeature = -> Chamfer
  Direction = (0,0,-1)
  Length = 2.5
  Length2 = 5
  Profile = -> Sketch004
  ReferenceAxis = -> Sketch004 [N_Axis]
  Refine = true
  Suppressed = false
  Type = 0
FEATURE [PartDesign::Chamfer] Chamfer001
  Angle = 45
  Base = -> Pocket002 [Edge901,Edge900,Edge905,Edge904,Edge903,Edge902,Edge913,Edge912,Edge917,Edge916,Edge915,Edge914,Edge895,Edge894,Edge899,Edge898,Edge897,Edge896,Edge907,Edge906,Edge911,Edge910,Edge909,Edge908]
  BaseFeature = -> Pocket002
  ChamferType = 0
  FlipDirection = false
  Refine = true
  Size = 0.5
  Size2 = 1
  SupportTransform = false
  Suppressed = false
  UseAllEdges = false
FEATURE [PartDesign::Chamfer] Chamfer002
  Angle = 45
  Base = -> Chamfer001 [Edge134,Edge147,Edge148,Edge149]
  BaseFeature = -> Chamfer001
  ChamferType = 0
  FlipDirection = false
  Refine = true
  Size = 0.5
  Size2 = 1
  SupportTransform = false
  Suppressed = false
  UseAllEdges = false
FEATURE [Sketcher::SketchObject] Sketch005
  ArcFitTolerance = 1e-06
  AttachmentSupport = -> [Chamfer002]
  ExternalGeometry = -> [Chamfer002]
  FullyConstrained = true
  MakeInternals = false
  MapMode = 5
  Placement = pos=(0,0,10) rot=(0,0,1;0rad)
  sketch-geometry (1):
    g0: Circle CenterX=0 CenterY=0 CenterZ=0 NormalX=0 NormalY=0 NormalZ=1 AngleXU=0 Radius=5.2
  constraints (2):
    c: Diameter(g0) = 10.4
    c: Coincident(g0,g-1)
FEATURE [PartDesign::Pocket] Pocket003
  BaseFeature = -> Chamfer002
  Direction = (0,0,-1)
  Length = 4.2
  Length2 = 5
  Profile = -> Sketch005
  ReferenceAxis = -> Sketch005 [N_Axis]
  Refine = true
  Suppressed = false
  Type = 0
FEATURE [PartDesign::Chamfer] Chamfer003
  Angle = 45
  Base = -> Pocket003 [Edge45]
  BaseFeature = -> Pocket003
  ChamferType = 0
  FlipDirection = false
  Refine = true
  Size = 0.5
  Size2 = 1
  SupportTransform = false
  Suppressed = false
  UseAllEdges = false
FEATURE [PartDesign::Chamfer] Chamfer004
  Angle = 45
  Base = -> Chamfer003 [Edge131,Edge139]
  BaseFeature = -> Chamfer003
  ChamferType = 0
  FlipDirection = false
  Refine = true
  Size = 0.5
  Size2 = 1
  SupportTransform = false
  Suppressed = false
  UseAllEdges = false
FEATURE [PartDesign::Body] Body
  AllowCompound = false
  BaseFeature = -> TimingGear
  Group = -> [BaseFeature,Sketch,Pad,Sketch001,Sketch002,Pad001,Pocket,Sketch003,Pocket001,Chamfer,Sketch004,Pocket002,Chamfer001,Chamfer002,Sketch005,Pocket003,Chamfer003,Chamfer004]
  Origin = -> Origin
  Tip = -> Chamfer004
---- part pulleys/gt2_48T_pulley_double.FCStd = doc fcstd_6ef7e6a60fe6 ----
FCSTD DOCUMENT  (FreeCAD 1.0R39109 (Git))
Label: gt2_48T_pulley_double
License: All rights reserved
LicenseURL: https://en.wikipedia.org/wiki/All_rights_reserved
objects: Sketcher::SketchObject×8, PartDesign::Pocket×5, PartDesign::Pad×3, PartDesign::Chamfer×2, Part::FeaturePython×1, PartDesign::FeatureBase×1, PartDesign::Mirrored×1, PartDesign::Body×1
note: 52 computed .brp shape members not serialized (recipe doc carries the construction recipe); baked Part::Feature solids carry a one-line shape summary decoded from their .brp

FEATURE [Part::FeaturePython] TimingGear  # WARN: FeaturePython — macro-defined, semantics opaque (R4)
  AttacherType = Attacher::AttachEngine3D
  h = 0.75
  height = 8
  num_teeth = 48
  offset = 0.4
  pitch = 2
  r0 = 0.555
  r1 = 1
  rs = 0.15
  type = 0
  u = 0.254
  version = 1.3.0
FEATURE [PartDesign::FeatureBase] BaseFeature
  BaseFeature = -> TimingGear
  Suppressed = false
FEATURE [Sketcher::SketchObject] Sketch
  ArcFitTolerance = 1e-06
  AttachmentSupport = -> [BaseFeature]
  FullyConstrained = true
  MakeInternals = false
  MapMode = 5
  Placement = pos=(0,0,0) rot=(1,0,0;3.14159rad)
  sketch-geometry (1):
    g0: Circle CenterX=0 CenterY=0 CenterZ=0 NormalX=0 NormalY=0 NormalZ=1 AngleXU=0 Radius=19
  constraints (2):
    c: Diameter(g0) = 38
    c: Coincident(g0,g-1)
FEATURE [PartDesign::Pad] Pad
  BaseFeature = -> BaseFeature
  Direction = (0,0,-1)
  Length = 1
  Length2 = 10
  Profile = -> Sketch
  ReferenceAxis = -> Sketch [N_Axis]
  Refine = true
  Suppressed = false
  Type = 0
FEATURE [Sketcher::SketchObject] Sketch001
  ArcFitTolerance = 1e-06
  AttachmentSupport = -> [Pad]
  FullyConstrained = false
  MakeInternals = false
  MapMode = 5
  Placement = pos=(0,0,-1) rot=(1,0,0;3.14159rad)
  sketch-geometry (6):
    g0: Circle [constr] CenterX=0 CenterY=0 CenterZ=0 NormalX=0 NormalY=0 NormalZ=1 AngleXU=0 Radius=11
    g1: LineSegment [constr] StartX=0 StartY=0 StartZ=0 EndX=0 EndY=11 EndZ=0
    g2: Circle CenterX=0 CenterY=11 CenterZ=0 NormalX=0 NormalY=0 NormalZ=1 AngleXU=0 Radius=1.25
    g3: Circle CenterX=-11 CenterY=0 CenterZ=0 NormalX=0 NormalY=0 NormalZ=1 AngleXU=0 Radius=1.25
    g4: Circle CenterX=0 CenterY=-11 CenterZ=0 NormalX=0 NormalY=0 NormalZ=1 AngleXU=0 Radius=1.25
    g5: Circle CenterX=11 CenterY=0 CenterZ=0 NormalX=0 NormalY=0 NormalZ=1 AngleXU=0 Radius=1.25
  constraints (10):
    c: Diameter(g0) = 22
    c: Coincident(g0,g-1)
    c: Coincident(g1,g0)
    c: PointOnObject(g1,g0)
    c: Vertical(g1)
    c: Coincident(g2,g1)
    c: Diameter(g2) = 2.5
    c: Diameter(g3) = 2.5
    c: Diameter(g4) = 2.5
    c: Diameter(g5) = 2.5
FEATURE [Sketcher::SketchObject] Sketch002
  ArcFitTolerance = 1e-06
  AttachmentSupport = -> [Pad]
  ExternalGeometry = -> [Pad]
  FullyConstrained = true
  MakeInternals = false
  MapMode = 5
  Placement = pos=(0,0,8) rot=(0,0,1;0rad)
  sketch-geometry (1):
    g0: Circle CenterX=0 CenterY=0 CenterZ=0 NormalX=0 NormalY=0 NormalZ=1 AngleXU=0 Radius=19
  constraints (2):
    c: Coincident(g0,g-1)
    c: Diameter(g0) = 38
FEATURE [PartDesign::Pad] Pad001
  BaseFeature = -> Pad
  Direction = (0,0,1)
  Length = 2
  Length2 = 10
  Profile = -> Sketch002
  ReferenceAxis = -> Sketch002 [N_Axis]
  Refine = true
  Suppressed = false
  Type = 0
FEATURE [PartDesign::Pocket] Pocket
  BaseFeature = -> Pad001
  Direction = (0,0,1)
  Length = 29
  Length2 = 5
  Profile = -> Sketch001
  ReferenceAxis = -> Sketch001 [N_Axis]
  Refine = true
  Suppressed = false
  Type = 0
FEATURE [Sketcher::SketchObject] Sketch003
  ArcFitTolerance = 1e-06
  AttachmentSupport = -> [Pocket]
  FullyConstrained = true
  MakeInternals = false
  MapMode = 5
  Placement = pos=(0,0,-1) rot=(1,0,0;3.14159rad)
  sketch-geometry (1):
    g0: Circle CenterX=0 CenterY=0 CenterZ=0 NormalX=0 NormalY=0 NormalZ=1 AngleXU=0 Radius=5
  constraints (2):
    c: Diameter(g0) = 10
    c: Coincident(g0,g-1)
FEATURE [PartDesign::Pocket] Pocket001
  BaseFeature = -> Pocket
  Direction = (0,0,1)
  Length = 17
  Length2 = 5
  Profile = -> Sketch003
  ReferenceAxis = -> Sketch003 [N_Axis]
  Refine = true
  Suppressed = false
  Type = 0
FEATURE [PartDesign::Chamfer] Chamfer
  Angle = 45
  Base = -> Pocket001 [Edge870,Edge297,Edge11,Edge878,Edge879,Edge876,Edge877,Edge880]
  BaseFeature = -> Pocket001
  ChamferType = 0
  FlipDirection = false
  Refine = true
  Size = 0.5
  Size2 = 1
  SupportTransform = false
  Suppressed = false
  UseAllEdges = false
FEATURE [PartDesign::Mirrored] Mirrored
  BaseFeature = -> Chamfer
  MirrorPlane = -> Chamfer [Face293]
  Refine = true
  Suppressed = false
  TransformMode = 1
FEATURE [Sketcher::SketchObject] Sketch004
  ArcFitTolerance = 1e-06
  AttachmentSupport = -> [Mirrored]
  ExternalGeometry = -> [Mirrored]
  FullyConstrained = false
  MakeInternals = false
  MapMode = 5
  Placement = pos=(0,0,-12) rot=(1,0,0;3.14159rad)
  sketch-geometry (5):
    g0: Circle CenterX=0 CenterY=0 CenterZ=0 NormalX=0 NormalY=0 NormalZ=1 AngleXU=0 Radius=7.1969
    g1: Circle CenterX=0 CenterY=11 CenterZ=0 NormalX=0 NormalY=0 NormalZ=1 AngleXU=0 Radius=2.72357
    g2: Circle CenterX=-11 CenterY=0 CenterZ=0 NormalX=0 NormalY=0 NormalZ=1 AngleXU=0 Radius=2.65153
    g3: Circle CenterX=0 CenterY=-11 CenterZ=0 NormalX=0 NormalY=0 NormalZ=1 AngleXU=0 Radius=3.2579
    g4: Circle CenterX=11 CenterY=0 CenterZ=0 NormalX=0 NormalY=0 NormalZ=1 AngleXU=0 Radius=3.02055
  constraints (5):
    c: Coincident(g0,g-1)
    c: Coincident(g1,g-3)
    c: Coincident(g2,g-4)
    c: Coincident(g3,g-5)
    c: Coincident(g4,g-6)
FEATURE [PartDesign::Pad] Pad002
  BaseFeature = -> Mirrored
  Direction = (0,0,-1)
  Length = 22
  Length2 = 10
  Profile = -> Sketch004
  ReferenceAxis = -> Sketch004 [N_Axis]
  Refine = true
  Reversed = true
  Suppressed = false
  Type = 0
FEATURE [Sketcher::SketchObject] Sketch005
  ArcFitTolerance = 1e-06
  AttachmentSupport = -> [Pad002]
  FullyConstrained = true
  MakeInternals = false
  MapMode = 5
  Placement = pos=(0,0,-12) rot=(1,0,0;3.14159rad)
  sketch-geometry (1):
    g0: Circle CenterX=0 CenterY=0 CenterZ=0 NormalX=0 NormalY=0 NormalZ=1 AngleXU=0 Radius=3
  constraints (2):
    c: Coincident(g0,g-1)
    c: Diameter(g0) = 6
FEATURE [PartDesign::Pocket] Pocket002
  BaseFeature = -> Pad002
  Direction = (0,0,1)
  Length = 5
  Length2 = 5
  Profile = -> Sketch005
  ReferenceAxis = -> Sketch005 [N_Axis]
  Refine = true
  Suppressed = false
  Type = 1
FEATURE [Sketcher::SketchObject] Sketch006
  ArcFitTolerance = 1e-06
  AttachmentSupport = -> [Pocket002]
  FullyConstrained = true
  MakeInternals = false
  MapMode = 5
  Placement = pos=(0,0,-12) rot=(1,0,0;3.14159rad)
  sketch-geometry (1):
    g0: Circle CenterX=0 CenterY=0 CenterZ=0 NormalX=0 NormalY=0 NormalZ=1 AngleXU=0 Radius=5.2
  constraints (2):
    c: Coincident(g0,g-1)
    c: Diameter(g0) = 10.4
FEATURE [PartDesign::Pocket] Pocket003
  BaseFeature = -> Pocket002
  Direction = (0,0,1)
  Length = 4
  Length2 = 5
  Profile = -> Sketch006
  ReferenceAxis = -> Sketch006 [N_Axis]
  Refine = true
  Suppressed = false
  Type = 0
FEATURE [Sketcher::SketchObject] Sketch007
  ArcFitTolerance = 1e-06
  AttachmentSupport = -> [Pocket003]
  FullyConstrained = true
  MakeInternals = false
  MapMode = 5
  Placement = pos=(0,0,10) rot=(0,0,1;0rad)
  sketch-geometry (1):
    g0: Circle CenterX=0 CenterY=0 CenterZ=0 NormalX=0 NormalY=0 NormalZ=1 AngleXU=0 Radius=5.2
  constraints (2):
    c: Coincident(g0,g-1)
    c: Diameter(g0) = 10.4
FEATURE [PartDesign::Pocket] Pocket004
  BaseFeature = -> Pocket003
  Direction = (0,0,-1)
  Length = 4
  Length2 = 5
  Profile = -> Sketch007
  ReferenceAxis = -> Sketch007 [N_Axis]
  Refine = true
  Suppressed = false
  Type = 0
FEATURE [PartDesign::Chamfer] Chamfer001
  Angle = 45
  Base = -> Pocket004 [Edge1754,Edge1746]
  BaseFeature = -> Pocket004
  ChamferType = 0
  FlipDirection = false
  Refine = true
  Size = 0.5
  Size2 = 1
  SupportTransform = false
  Suppressed = false
  UseAllEdges = false
FEATURE [PartDesign::Body] Body
  AllowCompound = false
  BaseFeature = -> TimingGear
  Group = -> [BaseFeature,Sketch,Pad,Sketch001,Sketch002,Pad001,Pocket,Sketch003,Pocket001,Chamfer,Mirrored,Sketch004,Pad002,Sketch005,Pocket002,Sketch006,Pocket003,Sketch007,Pocket004,Chamfer001]
  Origin = -> Origin
  Tip = -> Chamfer001
